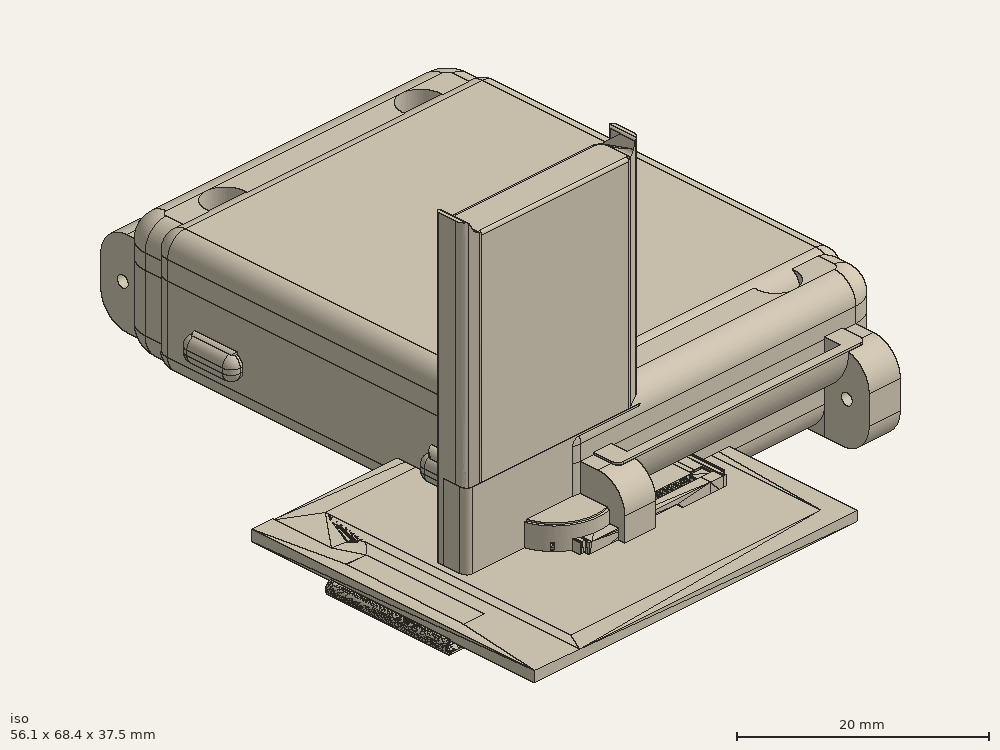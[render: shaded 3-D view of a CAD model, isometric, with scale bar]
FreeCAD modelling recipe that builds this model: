
FCSTD DOCUMENT  (FreeCAD 0.20R29177 +426 (Git))
Label: JJ-WATCHY_X
License: All rights reserved
LicenseURL: http://en.wikipedia.org/wiki/All_rights_reserved
objects: Part::Feature×80, App::Part×72, Sketcher::SketchObject×52, PartDesign::Pad×34, PartDesign::Pocket×27, PartDesign::Fillet×21, PartDesign::ShapeBinder×11, PartDesign::Body×8, PartDesign::Plane×4, Part::Part2DObjectPython×1, Part::Extrusion×1, PartDesign::FeatureBase×1, Mesh::Feature×1, Part::Fuse×1, Part::Cut×1
note: 324 computed .brp shape members not serialized (recipe doc carries the construction recipe); baked Part::Feature solids carry a one-line shape summary decoded from their .brp

FEATURE [Part::Feature] Part__Feature  label="SOLID (15)"
  shape: bbox 7.981 x 5.422 x 2.941 mm, 498 faces (baked)
FEATURE [App::Part] USB_Micro_B_Molex_47346_0001  label="USB_Micro-B_Molex_47346-0001"
  Group = -> [Part__Feature]
  Origin = -> Origin
  Placement = pos=(31.38,22.43,1.65) rot=(0,0,1;1.5708rad)
FEATURE [Part::Feature] Part__Feature001  label="SOLID"
  shape: bbox 1.6 x 0.8 x 0.8 mm, 28 faces (baked)
FEATURE [App::Part] C_0603_1608Metric
  Group = -> [Part__Feature001]
  Origin = -> Origin001
  Placement = pos=(5.16,37.71,1.65) rot=(0,0,1;0rad)
FEATURE [Part::Feature] Part__Feature002  label="SOLID (16)"
  shape: bbox 6.669 x 4.906 x 2.452 mm, 452 faces (baked)
FEATURE [App::Part] Button
  Group = -> [Part__Feature002]
  Origin = -> Origin002
  Placement = pos=(2.38,35.43,1.65) rot=(0,0,-1;1.5708rad)
FEATURE [Part::Feature] Part__Feature003  label="SOLID (16)001"
  shape: bbox 6.669 x 4.906 x 2.452 mm, 452 faces (baked)
FEATURE [App::Part] Button001
  Group = -> [Part__Feature003]
  Origin = -> Origin003
  Placement = pos=(2.38,8.73,1.65) rot=(0,0,-1;1.5708rad)
FEATURE [Part::Feature] Part__Feature004  label="SOLID (16)002"
  shape: bbox 6.669 x 4.906 x 2.452 mm, 452 faces (baked)
FEATURE [App::Part] Button002
  Group = -> [Part__Feature004]
  Origin = -> Origin004
  Placement = pos=(31.42,37.23,1.65) rot=(0,0,1;1.5708rad)
FEATURE [Part::Feature] Part__Feature005  label="SOLID (16)003"
  shape: bbox 6.669 x 4.906 x 2.452 mm, 452 faces (baked)
FEATURE [App::Part] Button003
  Group = -> [Part__Feature005]
  Origin = -> Origin005
  Placement = pos=(31.42,10.53,1.65) rot=(0,0,1;1.5708rad)
FEATURE [Part::Feature] Part__Feature006  label="SOLID (1)"
  shape: bbox 2 x 2 x 1.025 mm, 68 faces (baked)
FEATURE [App::Part] LGA_12_2x2mm_P0_5mm  label="LGA-12_2x2mm_P0.5mm"
  Group = -> [Part__Feature006]
  Origin = -> Origin006
  Placement = pos=(10.76,34.89,1.65) rot=(0,0,1;3.14159rad)
FEATURE [Part::Feature] Part__Feature007  label="COMPOUND (3)"
  shape: bbox 16.3 x 5.85 x 2.11 mm, 1280 faces, 17 solids (baked)
FEATURE [App::Part] FPC_24  label="FPC-24"
  Group = -> [Part__Feature007]
  Origin = -> Origin007
  Placement = pos=(11.025,19.09,1.65) rot=(0,0,1;0rad)
FEATURE [Part::Feature] Part__Feature008  label="SOLID (4)"
  shape: bbox 7.65 x 5.2 x 3.4 mm, 136 faces (baked)
FEATURE [App::Part] Molex_PicoBlade_53261_0271_1x02_1MP_P1_25mm_Horizontal  label="Molex_PicoBlade_53261-0271_1x02-1MP_P1.25mm_Horizontal"
  Group = -> [Part__Feature008]
  Origin = -> Origin008
  Placement = pos=(28.63,31.39,1.65) rot=(0,0,-1;1.5708rad)
FEATURE [Part::Feature] Part__Feature009  label="SOLID (2)"
  shape: bbox 1 x 0.5 x 0.35 mm, 26 faces (baked)
FEATURE [App::Part] R_0402_1005Metric
  Group = -> [Part__Feature009]
  Origin = -> Origin009
  Placement = pos=(31.7,28.28,1.65) rot=(0,0,1;1.5708rad)
FEATURE [Part::Feature] Part__Feature010  label="SOLID (5)"
  shape: bbox 4 x 4 x 1.1 mm, 158 faces (baked)
FEATURE [App::Part] QFN_24_1EP_4x4mm_P0_5mm_EP2_7x2_7mm  label="QFN-24-1EP_4x4mm_P0.5mm_EP2.7x2.7mm"
  Group = -> [Part__Feature010]
  Origin = -> Origin010
  Placement = pos=(25.76,24.38,1.65) rot=(0,0,1;0rad)
FEATURE [Part::Feature] Part__Feature011  label="SOLID (2)001"
  shape: bbox 1 x 0.5 x 0.35 mm, 26 faces (baked)
FEATURE [App::Part] R_0402_1005Metric001
  Group = -> [Part__Feature011]
  Origin = -> Origin011
  Placement = pos=(29.05,13.07,1.65) rot=(0,0,1;0rad)
FEATURE [Part::Feature] Part__Feature012  label="SOLID001"
  shape: bbox 1.6 x 0.8 x 0.8 mm, 28 faces (baked)
FEATURE [App::Part] C_0603_1608Metric001
  Group = -> [Part__Feature012]
  Origin = -> Origin012
  Placement = pos=(21.71,23.42,1.65) rot=(0,0,1;0rad)
FEATURE [Part::Feature] Part__Feature013  label="COMPOUND"
  shape: bbox 37.16 x 32.08 x 2.7 mm, 57 faces, 2 solids (baked)
FEATURE [App::Part] Display
  Group = -> [Part__Feature013]
  Origin = -> Origin013
  Placement = pos=(16.89,23.15,0.55) rot=(0.707107,0.707107,0;3.14159rad)
FEATURE [Part::Feature] Part__Feature014  label="SOLID002"
  shape: bbox 1.6 x 0.8 x 0.8 mm, 28 faces (baked)
FEATURE [App::Part] C_0603_1608Metric002
  Group = -> [Part__Feature014]
  Origin = -> Origin014
  Placement = pos=(15.42,35.06,1.65) rot=(0,0,1;1.5708rad)
FEATURE [Part::Feature] Part__Feature015  label="SOLID003"
  shape: bbox 1.6 x 0.8 x 0.8 mm, 28 faces (baked)
FEATURE [App::Part] C_0603_1608Metric003
  Group = -> [Part__Feature015]
  Origin = -> Origin015
  Placement = pos=(19.01,21.47,1.65) rot=(0,0,1;1.5708rad)
FEATURE [Part::Feature] Part__Feature016  label="SOLID (3)"
  shape: bbox 2 x 1.25 x 1.25 mm, 28 faces (baked)
FEATURE [App::Part] C_0805_2012Metric
  Group = -> [Part__Feature016]
  Origin = -> Origin016
  Placement = pos=(5.63,12.59,1.65) rot=(0,0,1;0rad)
FEATURE [Part::Feature] Part__Feature017  label="SOLID (3)001"
  shape: bbox 2 x 1.25 x 1.25 mm, 28 faces (baked)
FEATURE [App::Part] C_0805_2012Metric001
  Group = -> [Part__Feature017]
  Origin = -> Origin017
  Placement = pos=(6.63,6.34,1.65) rot=(0,0,1;0rad)
FEATURE [Part::Feature] Part__Feature018  label="SOLID004"
  shape: bbox 1.6 x 0.8 x 0.8 mm, 28 faces (baked)
FEATURE [App::Part] C_0603_1608Metric004
  Group = -> [Part__Feature018]
  Origin = -> Origin018
  Placement = pos=(13.81,21.47,1.65) rot=(0,0,1;1.5708rad)
FEATURE [Part::Feature] Part__Feature019  label="SOLID005"
  shape: bbox 1.6 x 0.8 x 0.8 mm, 28 faces (baked)
FEATURE [App::Part] C_0603_1608Metric005
  Group = -> [Part__Feature019]
  Origin = -> Origin019
  Placement = pos=(16.41,21.47,1.65) rot=(0,0,1;1.5708rad)
FEATURE [Part::Feature] Part__Feature020  label="SOLID006"
  shape: bbox 1.6 x 0.8 x 0.8 mm, 28 faces (baked)
FEATURE [App::Part] C_0603_1608Metric006
  Group = -> [Part__Feature020]
  Origin = -> Origin020
  Placement = pos=(17.71,21.47,1.65) rot=(0,0,1;1.5708rad)
FEATURE [Part::Feature] Part__Feature021  label="SOLID007"
  shape: bbox 1.6 x 0.8 x 0.8 mm, 28 faces (baked)
FEATURE [App::Part] C_0603_1608Metric007
  Group = -> [Part__Feature021]
  Origin = -> Origin021
  Placement = pos=(15.11,21.47,1.65) rot=(0,0,1;1.5708rad)
FEATURE [Part::Feature] Part__Feature022  label="SOLID008"
  shape: bbox 1.6 x 0.8 x 0.8 mm, 28 faces (baked)
FEATURE [App::Part] C_0603_1608Metric008
  Group = -> [Part__Feature022]
  Origin = -> Origin022
  Placement = pos=(12.46,21.47,1.65) rot=(0,0,1;1.5708rad)
FEATURE [Part::Feature] Part__Feature023  label="SOLID009"
  shape: bbox 1.6 x 0.8 x 0.8 mm, 28 faces (baked)
FEATURE [App::Part] C_0603_1608Metric009
  Group = -> [Part__Feature023]
  Origin = -> Origin023
  Placement = pos=(11.16,21.47,1.65) rot=(0,0,1;1.5708rad)
FEATURE [Part::Feature] Part__Feature024  label="SOLID (3)002"
  shape: bbox 2 x 1.25 x 1.25 mm, 28 faces (baked)
FEATURE [App::Part] C_0805_2012Metric002
  Group = -> [Part__Feature024]
  Origin = -> Origin024
  Placement = pos=(17.82,35.53,1.65) rot=(0,0,1;3.14159rad)
FEATURE [Part::Feature] Part__Feature025  label="SOLID (6)"
  shape: bbox 3.8 x 1.6 x 1.25 mm, 67 faces (baked)
FEATURE [App::Part] D_SOD_123  label="D_SOD-123"
  Group = -> [Part__Feature025]
  Origin = -> Origin025
  Placement = pos=(1.25,15.82,1.65) rot=(0,0,1;1.5708rad)
FEATURE [Part::Feature] Part__Feature026  label="SOLID (6)001"
  shape: bbox 3.8 x 1.6 x 1.25 mm, 67 faces (baked)
FEATURE [App::Part] D_SOD_123001  label="D_SOD-124"
  Group = -> [Part__Feature026]
  Origin = -> Origin026
  Placement = pos=(3.55,15.82,1.65) rot=(0,0,-1;1.5708rad)
FEATURE [Part::Feature] Part__Feature027  label="SOLID (6)002"
  shape: bbox 3.8 x 1.6 x 1.25 mm, 67 faces (baked)
FEATURE [App::Part] D_SOD_123002  label="D_SOD-125"
  Group = -> [Part__Feature027]
  Origin = -> Origin027
  Placement = pos=(5.85,15.82,1.65) rot=(0,0,-1;1.5708rad)
FEATURE [Part::Feature] Part__Feature028  label="SOLID (6)003"
  shape: bbox 3.8 x 1.6 x 1.25 mm, 67 faces (baked)
FEATURE [App::Part] D_SOD_123003  label="D_SOD-126"
  Group = -> [Part__Feature028]
  Origin = -> Origin028
  Placement = pos=(27.27,19.28,1.65) rot=(0,0,1;1.5708rad)
FEATURE [Part::Feature] Part__Feature029  label="SOLID (7)"
  shape: bbox 1.6 x 0.8 x 1.1 mm, 50 faces (baked)
FEATURE [App::Part] LED_0603_1608Metric
  Group = -> [Part__Feature029]
  Origin = -> Origin029
  Placement = pos=(33.04,30.53,1.65) rot=(0,0,1;1.5708rad)
FEATURE [Part::Feature] Part__Feature030  label="SOLID (8)"
  shape: bbox 3.5 x 1.6 x 1.1 mm, 27 faces (baked)
FEATURE [App::Part] D_SOD_123F  label="D_SOD-123F"
  Group = -> [Part__Feature030]
  Origin = -> Origin030
  Placement = pos=(4.91,34.705,1.65) rot=(0,0,-1;1.5708rad)
FEATURE [Part::Feature] Part__Feature031  label="SOLID (9)"
  shape: bbox 3.2 x 2.5 x 2.5 mm, 28 faces (baked)
FEATURE [App::Part] L_1210_3225Metric
  Group = -> [Part__Feature031]
  Origin = -> Origin031
  Placement = pos=(6.13,9.47,1.65) rot=(0,0,-1;1.5708rad)
FEATURE [Part::Feature] Part__Feature032  label="SOLID (10)"
  shape: bbox 2.5 x 3 x 1.2 mm, 76 faces (baked)
FEATURE [App::Part] SOT_23  label="SOT-23"
  Group = -> [Part__Feature032]
  Origin = -> Origin032
  Placement = pos=(28.1,9.03,1.65) rot=(0,0,-1;1.5708rad)
FEATURE [Part::Feature] Part__Feature033  label="SOLID (10)001"
  shape: bbox 2.5 x 3 x 1.2 mm, 76 faces (baked)
FEATURE [App::Part] SOT_23001  label="SOT-024"
  Group = -> [Part__Feature033]
  Origin = -> Origin033
  Placement = pos=(28.45,15.23,1.65) rot=(0,0,-1;1.5708rad)
FEATURE [Part::Feature] Part__Feature034  label="SOLID (10)002"
  shape: bbox 2.5 x 3 x 1.2 mm, 76 faces (baked)
FEATURE [App::Part] SOT_23002  label="SOT-025"
  Group = -> [Part__Feature034]
  Origin = -> Origin034
  Placement = pos=(7.81,35.31,1.65) rot=(0,0,1;3.14159rad)
FEATURE [Part::Feature] Part__Feature035  label="SOLID (2)002"
  shape: bbox 1 x 0.5 x 0.35 mm, 26 faces (baked)
FEATURE [App::Part] R_0402_1005Metric002
  Group = -> [Part__Feature035]
  Origin = -> Origin035
  Placement = pos=(16.97,34.19,1.65) rot=(0,0,1;3.14159rad)
FEATURE [Part::Feature] Part__Feature036  label="SOLID (2)003"
  shape: bbox 1 x 0.5 x 0.35 mm, 26 faces (baked)
FEATURE [App::Part] R_0402_1005Metric003
  Group = -> [Part__Feature036]
  Origin = -> Origin036
  Placement = pos=(22.55,26.67,1.65) rot=(0,0,1;1.5708rad)
FEATURE [Part::Feature] Part__Feature037  label="SOLID (2)004"
  shape: bbox 1 x 0.5 x 0.35 mm, 26 faces (baked)
FEATURE [App::Part] R_0402_1005Metric004
  Group = -> [Part__Feature037]
  Origin = -> Origin037
  Placement = pos=(23.91,27.48,1.65) rot=(0,0,1;3.14159rad)
FEATURE [Part::Feature] Part__Feature038  label="SOLID (2)005"
  shape: bbox 1 x 0.5 x 0.35 mm, 26 faces (baked)
FEATURE [App::Part] R_0402_1005Metric005
  Group = -> [Part__Feature038]
  Origin = -> Origin038
  Placement = pos=(27.15,13.07,1.65) rot=(0,0,1;3.14159rad)
FEATURE [Part::Feature] Part__Feature039  label="SOLID (2)006"
  shape: bbox 1 x 0.5 x 0.35 mm, 26 faces (baked)
FEATURE [App::Part] R_0402_1005Metric006
  Group = -> [Part__Feature039]
  Origin = -> Origin039
  Placement = pos=(28.66,36.44,1.65) rot=(0,0,1;0rad)
FEATURE [Part::Feature] Part__Feature040  label="SOLID (2)007"
  shape: bbox 1 x 0.5 x 0.35 mm, 26 faces (baked)
FEATURE [App::Part] R_0402_1005Metric007
  Group = -> [Part__Feature040]
  Origin = -> Origin040
  Placement = pos=(6.69,32.68,1.65) rot=(0,0,-1;1.5708rad)
FEATURE [Part::Feature] Part__Feature041  label="SOLID (2)008"
  shape: bbox 1 x 0.5 x 0.35 mm, 26 faces (baked)
FEATURE [App::Part] R_0402_1005Metric008
  Group = -> [Part__Feature041]
  Origin = -> Origin041
  Placement = pos=(29.05,11.28,1.65) rot=(0,0,1;3.14159rad)
FEATURE [Part::Feature] Part__Feature042  label="SOLID (2)009"
  shape: bbox 1 x 0.5 x 0.35 mm, 26 faces (baked)
FEATURE [App::Part] R_0402_1005Metric009
  Group = -> [Part__Feature042]
  Origin = -> Origin042
  Placement = pos=(27.15,11.28,1.65) rot=(0,0,1;3.14159rad)
FEATURE [Part::Feature] Part__Feature043  label="SOLID (2)010"
  shape: bbox 1 x 0.5 x 0.35 mm, 26 faces (baked)
FEATURE [App::Part] R_0402_1005Metric010
  Group = -> [Part__Feature043]
  Origin = -> Origin043
  Placement = pos=(4.35,6.34,1.65) rot=(0,0,1;1.5708rad)
FEATURE [Part::Feature] Part__Feature044  label="SOLID (2)011"
  shape: bbox 1 x 0.5 x 0.35 mm, 26 faces (baked)
FEATURE [App::Part] R_0402_1005Metric011
  Group = -> [Part__Feature044]
  Origin = -> Origin044
  Placement = pos=(30.8,28.28,1.65) rot=(0,0,1;1.5708rad)
FEATURE [Part::Feature] Part__Feature045  label="SOLID (2)012"
  shape: bbox 1 x 0.5 x 0.35 mm, 26 faces (baked)
FEATURE [App::Part] R_0402_1005Metric012
  Group = -> [Part__Feature045]
  Origin = -> Origin045
  Placement = pos=(29.32,17.4,1.65) rot=(0,0,1;3.14159rad)
FEATURE [Part::Feature] Part__Feature046  label="SOLID (2)013"
  shape: bbox 1 x 0.5 x 0.35 mm, 26 faces (baked)
FEATURE [App::Part] R_0402_1005Metric013
  Group = -> [Part__Feature046]
  Origin = -> Origin046
  Placement = pos=(33.24,28.28,1.65) rot=(0,0,-1;1.5708rad)
FEATURE [Part::Feature] Part__Feature047  label="SOLID (2)014"
  shape: bbox 1 x 0.5 x 0.35 mm, 26 faces (baked)
FEATURE [App::Part] R_0402_1005Metric014
  Group = -> [Part__Feature047]
  Origin = -> Origin047
  Placement = pos=(7.75,32.68,1.65) rot=(0,0,-1;1.5708rad)
FEATURE [Part::Feature] Part__Feature048  label="SOLID (13)"
  shape: bbox 7 x 7 x 0.77 mm, 302 faces (baked)
FEATURE [App::Part] QFN_48_1EP_7x7mm_P0_5mm_EP5_15x5_15mm  label="QFN-48-1EP_7x7mm_P0.5mm_EP5.15x5.15mm"
  Group = -> [Part__Feature048]
  Origin = -> Origin048
  Placement = pos=(17.7737,29.6588,1.65) rot=(0,0,-1;1.5708rad)
FEATURE [Part::Feature] Part__Feature049  label="SOLID (11)"
  shape: bbox 2.8 x 2.9 x 1.55 mm, 109 faces (baked)
FEATURE [App::Part] SOT_23_5  label="SOT-23-5"
  Group = -> [Part__Feature049]
  Origin = -> Origin049
  Placement = pos=(24.66,19.88,1.65) rot=(0,0,-1;1.5708rad)
FEATURE [Part::Feature] Part__Feature050  label="SOLID (11)001"
  shape: bbox 2.8 x 2.9 x 1.55 mm, 109 faces (baked)
FEATURE [App::Part] SOT_23_5001  label="SOT-23-006"
  Group = -> [Part__Feature050]
  Origin = -> Origin050
  Placement = pos=(32,15.93,1.65) rot=(0,0,-1;1.5708rad)
FEATURE [Part::Feature] Part__Feature051  label="SOLID (12)"
  shape: bbox 2 x 2 x 1.05 mm, 118 faces (baked)
FEATURE [App::Part] SOT_363_SC_70_6  label="SOT-363_SC-70-6"
  Group = -> [Part__Feature051]
  Origin = -> Origin051
  Placement = pos=(21.31,21.47,1.65) rot=(0,0,1;3.14159rad)
FEATURE [Part::Feature] Part__Feature052  label="SOLID (14)"
  shape: bbox 6 x 4.9 x 1.75 mm, 156 faces (baked)
FEATURE [App::Part] SOIC_8_3_9x4_9mm_P1_27mm  label="SOIC-8_3.9x4.9mm_P1.27mm"
  Group = -> [Part__Feature052]
  Origin = -> Origin052
  Placement = pos=(11.07,29.81,1.65) rot=(0,0,1;1.5708rad)
FEATURE [Part::Feature] Part__Feature053  label="SOLID (2)015"
  shape: bbox 1 x 0.5 x 0.35 mm, 26 faces (baked)
FEATURE [App::Part] R_0402_1005Metric015
  Group = -> [Part__Feature053]
  Origin = -> Origin053
  Placement = pos=(7.75,30.52,1.65) rot=(0,0,-1;1.5708rad)
FEATURE [Part::Feature] Part__Feature054  label="COMPOUND (1)"
  shape: bbox 13 x 10 x 2.5 mm, 15 faces, 3 solids (baked)
FEATURE [App::Part] PagerMotor
  Group = -> [Part__Feature054]
  Origin = -> Origin054
  Placement = pos=(5.45,22.955,5.15) rot=(0.819152,-0.573576,0;3.14159rad)
FEATURE [Part::Feature] Part__Feature055  label="COMPOUND (2)"
  shape: bbox 33.8 x 45.96 x 1 mm, 46 faces (baked)
FEATURE [App::Part] Watchy_Fixed_Dimensions_v1  label="Watchy Fixed Dimensions v1"
  Group = -> [USB_Micro_B_Molex_47346_0001,C_0603_1608Metric,Button,Button001,Button002,Button003,LGA_12_2x2mm_P0_5mm,FPC_24,Molex_PicoBlade_53261_0271_1x02_1MP_P1_25mm_Horizontal,R_0402_1005Metric,QFN_24_1EP_4x4mm_P0_5mm_EP2_7x2_7mm,R_0402_1005Metric001,C_0603_1608Metric001,Display,C_0603_1608Metric002,C_0603_1608Metric003,C_0805_2012Metric,C_0805_2012Metric001,C_0603_1608Metric004,C_0603_1608Metric005,+36 more]
  Origin = -> Origin055
  Placement = pos=(0,0,-0.43) rot=(0,0,1;0rad)
FEATURE [Sketcher::SketchObject] Sketch
  FullyConstrained = true
  MapMode = 5
  Placement = pos=(0,0,0) rot=(0,1,0;3.14159rad)
  Support = -> [XY_Plane056]
  sketch-geometry (4):
    g0: LineSegment StartX=-32.81 StartY=41.31 StartZ=0 EndX=-0.98 EndY=41.31 EndZ=0
    g1: LineSegment StartX=-0.98 StartY=41.31 StartZ=0 EndX=-0.98 EndY=10.07 EndZ=0
    g2: LineSegment StartX=-0.98 StartY=10.07 StartZ=0 EndX=-32.81 EndY=10.07 EndZ=0
    g3: LineSegment StartX=-32.81 StartY=10.07 StartZ=0 EndX=-32.81 EndY=41.31 EndZ=0
  constraints (12):
    c: Coincident(g0,g1)
    c: Coincident(g1,g2)
    c: Coincident(g2,g3)
    c: Coincident(g3,g0)
    c: Horizontal(g0)
    c: Horizontal(g2)
    c: Vertical(g1)
    c: Vertical(g3)
    c: DistanceX(g0,g0) = 31.83
    c: DistanceY(g1,g1) = 31.24
    c: DistanceY(g-1,g1) = 10.07
    c: DistanceX(g1,g-1) = 0.98
FEATURE [PartDesign::Pad] Pad
  Direction = (0,0,-1)
  Length = 1.5
  Length2 = 10
  Profile = -> Sketch
  ReferenceAxis = -> Sketch [N_Axis]
  Type = 0
FEATURE [PartDesign::Fillet] Fillet
  Base = -> Pad [Edge1,Edge2,Edge5,Edge8]
  BaseFeature = -> Pad
  Radius = 1
  SupportTransform = false
  UseAllEdges = false
FEATURE [PartDesign::Pocket] Pocket
  BaseFeature = -> Fillet
  Direction = (0,0,-1)
  Length = 0.9
  Length2 = 5
  Profile = -> Fillet [Face2]
  Type = 0
FEATURE [PartDesign::ShapeBinder] ReferencePocket
  Placement = pos=(0,0,-1.5) rot=(0,0,1;0rad)
  Support = -> [Pocket]
  TraceSupport = false
FEATURE [PartDesign::Plane] DatumPlane
  Length = 75.1964
  MapMode = 5
  Placement = pos=(0,0,-1.5) rot=(1,0,0;3.14159rad)
  ResizeMode = 0
  Support = -> [ReferencePocket]
  Width = 91.2964
FEATURE [Sketcher::SketchObject] Sketch001
  ExternalGeometry = -> [ReferencePocket]
  FullyConstrained = true
  MapMode = 5
  Placement = pos=(0,0,-1.5) rot=(1,0,0;3.14159rad)
  Support = -> [DatumPlane]
  sketch-geometry (5):
    g0: LineSegment StartX=-1.6 StartY=1.5 StartZ=0 EndX=35.4 EndY=1.5 EndZ=0
    g1: LineSegment StartX=35.4 StartY=1.5 StartZ=0 EndX=35.4 EndY=-47.5 EndZ=0
    g2: LineSegment StartX=35.4 StartY=-47.5 StartZ=0 EndX=-1.6 EndY=-47.5 EndZ=0
    g3: LineSegment StartX=-1.6 StartY=-47.5 StartZ=0 EndX=-1.6 EndY=1.5 EndZ=0
    g4: GeomPoint X=16.9 Y=-23 Z=0
  constraints (13):
    c: Coincident(g0,g1)
    c: Coincident(g1,g2)
    c: Coincident(g2,g3)
    c: Coincident(g3,g0)
    c: Horizontal(g0)
    c: Horizontal(g2)
    c: Vertical(g1)
    c: Vertical(g3)
    c: DistanceX(g0,g0) = 37
    c: DistanceY(g1,g1) = 49
    c: DistanceX(g-1,g4) = 16.9
    c: DistanceY(g4,g-1) = 23
    c: Symmetric(g2,g0,g4)
FEATURE [PartDesign::Pad] Pad001
  Direction = (0,0,-1)
  Length = 1
  Length2 = 8
  Placement = pos=(0,0,-1.5) rot=(1,0,0;3.14159rad)
  Profile = -> Sketch001
  ReferenceAxis = -> Sketch001 [N_Axis]
  Type = 4
FEATURE [Sketcher::SketchObject] Sketch002
  FullyConstrained = true
  MapMode = 5
  Placement = pos=(0,0,-2.5) rot=(1,0,0;3.14159rad)
  Support = -> [Pad001]
  sketch-geometry (5):
    g0: LineSegment StartX=3 StartY=-12.3 StartZ=0 EndX=31 EndY=-12.3 EndZ=0
    g1: LineSegment StartX=31 StartY=-12.3 StartZ=0 EndX=31 EndY=-39.3 EndZ=0
    g2: LineSegment StartX=31 StartY=-39.3 StartZ=0 EndX=3 EndY=-39.3 EndZ=0
    g3: LineSegment StartX=3 StartY=-39.3 StartZ=0 EndX=3 EndY=-12.3 EndZ=0
    g4: GeomPoint X=17 Y=-25.8 Z=0
  constraints (13):
    c: Coincident(g0,g1)
    c: Coincident(g1,g2)
    c: Coincident(g2,g3)
    c: Coincident(g3,g0)
    c: Horizontal(g0)
    c: Horizontal(g2)
    c: Vertical(g1)
    c: Vertical(g3)
    c: DistanceX(g0,g0) = 28
    c: DistanceY(g1,g1) = 27
    c: DistanceX(g-1,g4) = 17
    c: DistanceY(g4,g-1) = 25.8
    c: Symmetric(g2,g0,g4)
FEATURE [PartDesign::Pocket] Pocket001
  BaseFeature = -> Pad001
  Direction = (0,-1e-16,1)
  Length = 1
  Length2 = 5
  Placement = pos=(0,0,-1.5) rot=(1,0,0;3.14159rad)
  Profile = -> Sketch002
  ReferenceAxis = -> Sketch002 [N_Axis]
  Type = 0
FEATURE [Sketcher::SketchObject] Sketch003
  ExternalGeometry = -> [Pocket001]
  FullyConstrained = true
  MapMode = 5
  Placement = pos=(0,0,6.5) rot=(0,0,1;0rad)
  Support = -> [Pocket001]
  sketch-geometry (5):
    g0: LineSegment StartX=-0.6 StartY=46.5 StartZ=0 EndX=-0.6 EndY=-0.5 EndZ=0
    g1: LineSegment StartX=-0.6 StartY=-0.5 StartZ=0 EndX=34.4 EndY=-0.5 EndZ=0
    g2: LineSegment StartX=34.4 StartY=-0.5 StartZ=0 EndX=34.4 EndY=46.5 EndZ=0
    g3: LineSegment StartX=34.4 StartY=46.5 StartZ=0 EndX=-0.6 EndY=46.5 EndZ=0
    g4: Circle CenterX=16.9 CenterY=23 CenterZ=0 NormalX=0 NormalY=0 NormalZ=1 AngleXU=0 Radius=29.3002
  constraints (14):
    c: Coincident(g0,g1)
    c: Coincident(g1,g2)
    c: Coincident(g2,g3)
    c: Coincident(g3,g0)
    c: PointOnObject(g0,g4)
    c: PointOnObject(g1,g4)
    c: PointOnObject(g2,g4)
    c: PointOnObject(g3,g4)
    c: Horizontal(g3)
    c: Horizontal(g1)
    c: Vertical(g2)
    c: DistanceX(g3,g3) = 35
    c: DistanceY(g2,g2) = 47
    c: Symmetric(g-3,g-4,g4)
FEATURE [PartDesign::Pocket] Pocket002
  BaseFeature = -> Pocket001
  Direction = (0,2e-16,-1)
  Length = 7
  Length2 = 5
  Placement = pos=(0,0,-1.5) rot=(1,0,0;3.14159rad)
  Profile = -> Sketch003
  ReferenceAxis = -> Sketch003 [N_Axis]
  Type = 0
FEATURE [Sketcher::SketchObject] Sketch004
  ExternalGeometry = -> [ReferencePocket]
  FullyConstrained = true
  MapMode = 5
  Placement = pos=(0,-2e-16,-0.5) rot=(0,0,1;0rad)
  Support = -> [Pocket002]
  sketch-geometry (4):
    g0: LineSegment StartX=0.48 StartY=41.81 StartZ=0 EndX=33.31 EndY=41.81 EndZ=0
    g1: LineSegment StartX=33.31 StartY=41.81 StartZ=0 EndX=33.31 EndY=9.57 EndZ=0
    g2: LineSegment StartX=33.31 StartY=9.57 StartZ=0 EndX=0.48 EndY=9.57 EndZ=0
    g3: LineSegment StartX=0.48 StartY=9.57 StartZ=0 EndX=0.48 EndY=41.81 EndZ=0
  constraints (12):
    c: Coincident(g0,g1)
    c: Coincident(g1,g2)
    c: Coincident(g2,g3)
    c: Coincident(g3,g0)
    c: Horizontal(g0)
    c: Horizontal(g2)
    c: Vertical(g1)
    c: Vertical(g3)
    c: DistanceX(g0,g-4) = 0.5
    c: DistanceX(g-6,g0) = 0.5
    c: DistanceY(g-3,g0) = 0.5
    c: DistanceY(g1,g-5) = 0.5
FEATURE [PartDesign::Pocket] Pocket003
  BaseFeature = -> Pocket002
  Direction = (0,4e-16,-1)
  Length = 1
  Length2 = 5
  Placement = pos=(0,0,-1.5) rot=(1,0,0;3.14159rad)
  Profile = -> Sketch004
  ReferenceAxis = -> Sketch004 [N_Axis]
  Type = 0
FEATURE [Sketcher::SketchObject] Sketch005
  FullyConstrained = true
  MapMode = 5
  Placement = pos=(34.4,0,-1.5) rot=(0.57735,0.57735,-0.57735;4.18879rad)
  Support = -> [Pocket003]
  sketch-geometry (4):
    g0: LineSegment StartX=18.2 StartY=-2.15 StartZ=0 EndX=26.7 EndY=-2.15 EndZ=0
    g1: LineSegment StartX=26.7 StartY=-2.15 StartZ=0 EndX=26.7 EndY=-5.75 EndZ=0
    g2: LineSegment StartX=26.7 StartY=-5.75 StartZ=0 EndX=18.2 EndY=-5.75 EndZ=0
    g3: LineSegment StartX=18.2 StartY=-5.75 StartZ=0 EndX=18.2 EndY=-2.15 EndZ=0
  constraints (12):
    c: Coincident(g0,g1)
    c: Coincident(g1,g2)
    c: Coincident(g2,g3)
    c: Coincident(g3,g0)
    c: Horizontal(g0)
    c: Horizontal(g2)
    c: Vertical(g1)
    c: Vertical(g3)
    c: DistanceX(g2,g2) = 8.5
    c: DistanceY(g1,g1) = 3.6
    c: DistanceX(g-1,g0) = 18.2
    c: DistanceY(g0,g-1) = 2.15
FEATURE [PartDesign::Pocket] Pocket004
  BaseFeature = -> Pocket003
  Direction = (1,0,0)
  Length = 5
  Length2 = 5
  Placement = pos=(0,0,-1.5) rot=(1,0,0;3.14159rad)
  Profile = -> Sketch005
  ReferenceAxis = -> Sketch005 [N_Axis]
  Type = 0
FEATURE [Sketcher::SketchObject] Sketch006
  ExternalGeometry = -> [Pocket004]
  FullyConstrained = true
  MapMode = 5
  Placement = pos=(0,0,6.5) rot=(0,0,1;0rad)
  Support = -> [Pocket004]
  sketch-geometry (20):
    g0: LineSegment StartX=-1 StartY=37.83 StartZ=0 EndX=-0.6 EndY=37.83 EndZ=0
    g1: LineSegment StartX=-0.6 StartY=37.83 StartZ=0 EndX=-0.6 EndY=34.83 EndZ=0
    g2: LineSegment StartX=-0.6 StartY=34.83 StartZ=0 EndX=-1 EndY=34.83 EndZ=0
    g3: LineSegment StartX=-1 StartY=34.83 StartZ=0 EndX=-1 EndY=37.83 EndZ=0
    g4: LineSegment StartX=34.4 StartY=37.83 StartZ=0 EndX=34.8 EndY=37.83 EndZ=0
    g5: LineSegment StartX=34.8 StartY=37.83 StartZ=0 EndX=34.8 EndY=34.83 EndZ=0
    g6: LineSegment StartX=34.8 StartY=34.83 StartZ=0 EndX=34.4 EndY=34.83 EndZ=0
    g7: LineSegment StartX=34.4 StartY=34.83 StartZ=0 EndX=34.4 EndY=37.83 EndZ=0
    g8: LineSegment StartX=34.4 StartY=8.13 StartZ=0 EndX=34.8 EndY=8.13 EndZ=0
    g9: LineSegment StartX=34.8 StartY=8.13 StartZ=0 EndX=34.8 EndY=11.13 EndZ=0
    g10: LineSegment StartX=34.8 StartY=11.13 StartZ=0 EndX=34.4 EndY=11.13 EndZ=0
    g11: LineSegment StartX=34.4 StartY=11.13 StartZ=0 EndX=34.4 EndY=8.13 EndZ=0
    g12: LineSegment StartX=-1 StartY=11.13 StartZ=0 EndX=-0.6 EndY=11.13 EndZ=0
    g13: LineSegment StartX=-0.6 StartY=11.13 StartZ=0 EndX=-0.6 EndY=8.13 EndZ=0
    g14: LineSegment StartX=-0.6 StartY=8.13 StartZ=0 EndX=-1 EndY=8.13 EndZ=0
    g15: LineSegment StartX=-1 StartY=8.13 StartZ=0 EndX=-1 EndY=11.13 EndZ=0
    g16: Circle CenterX=-0.8 CenterY=9.63 CenterZ=0 NormalX=0 NormalY=0 NormalZ=1 AngleXU=0 Radius=1.51327
    g17: Circle CenterX=34.6 CenterY=9.63 CenterZ=0 NormalX=0 NormalY=0 NormalZ=1 AngleXU=0 Radius=1.51327
    g18: Circle CenterX=34.6 CenterY=36.33 CenterZ=0 NormalX=0 NormalY=0 NormalZ=1 AngleXU=0 Radius=1.51327
    g19: Circle CenterX=-0.8 CenterY=36.33 CenterZ=0 NormalX=0 NormalY=0 NormalZ=1 AngleXU=0 Radius=1.51327
  constraints (60):
    c: Coincident(g0,g1)
    c: Coincident(g1,g2)
    c: Coincident(g2,g3)
    c: Coincident(g3,g0)
    c: Horizontal(g0)
    c: Horizontal(g2)
    c: Vertical(g1)
    c: Vertical(g3)
    c: PointOnObject(g0,g-3)
    c: DistanceX(g0,g0) = 0.4
    c: DistanceY(g3,g3) = 3
    c: Coincident(g4,g5)
    c: Coincident(g5,g6)
    c: Coincident(g6,g7)
    c: Coincident(g7,g4)
    c: Horizontal(g4)
    c: Horizontal(g6)
    c: Vertical(g5)
    c: Vertical(g7)
    c: Coincident(g8,g9)
    c: Coincident(g9,g10)
    c: Coincident(g10,g11)
    c: Coincident(g11,g8)
    c: Horizontal(g8)
    c: Horizontal(g10)
    c: Vertical(g9)
    c: Vertical(g11)
    c: Coincident(g12,g13)
    c: Coincident(g13,g14)
    c: Coincident(g14,g15)
    c: Coincident(g15,g12)
    c: Horizontal(g12)
    c: Horizontal(g14)
    c: Vertical(g13)
    c: Vertical(g15)
    c: Equal(g0,g12)
    c: Equal(g12,g4)
    c: Equal(g4,g8)
    c: Equal(g3,g13)
    c: Equal(g13,g5)
    c: Equal(g5,g9)
    c: PointOnObject(g12,g-3)
    c: PointOnObject(g4,g-4)
    c: PointOnObject(g8,g-4)
    c: PointOnObject(g12,g16)
    c: PointOnObject(g12,g16)
    c: PointOnObject(g14,g16)
    c: DistanceY(g-1,g16) = 9.63
    c: PointOnObject(g9,g17)
    c: PointOnObject(g10,g17)
    c: PointOnObject(g8,g17)
    c: PointOnObject(g4,g18)
    c: PointOnObject(g4,g18)
    c: PointOnObject(g5,g18)
    c: PointOnObject(g0,g19)
    c: PointOnObject(g0,g19)
    c: PointOnObject(g2,g19)
    c: DistanceY(g-1,g19) = 36.33
    c: DistanceY(g-1,g18) = 36.33
    c: DistanceY(g-1,g17) = 9.63
FEATURE [PartDesign::Pocket] Pocket005
  BaseFeature = -> Pocket004
  Direction = (0,0,-1)
  Length = 5.5
  Length2 = 5
  Placement = pos=(0,0,-1.5) rot=(1,0,0;3.14159rad)
  Profile = -> Sketch006
  ReferenceAxis = -> Sketch006 [N_Axis]
  Type = 0
FEATURE [Sketcher::SketchObject] Sketch007
  FullyConstrained = true
  MapMode = 5
  Placement = pos=(-1.6,0,-1.5) rot=(0.57735,0.57735,-0.57735;4.18879rad)
  Support = -> [Pocket005]
  sketch-geometry (8):
    g0: LineSegment StartX=7.23 StartY=-3.5 StartZ=0 EndX=12.03 EndY=-3.5 EndZ=0
    g1: LineSegment StartX=12.03 StartY=-3.5 StartZ=0 EndX=12.03 EndY=-5.3 EndZ=0
    g2: LineSegment StartX=12.03 StartY=-5.3 StartZ=0 EndX=7.23 EndY=-5.3 EndZ=0
    g3: LineSegment StartX=7.23 StartY=-5.3 StartZ=0 EndX=7.23 EndY=-3.5 EndZ=0
    g4: LineSegment StartX=33.9 StartY=-3.1 StartZ=0 EndX=38.7 EndY=-3.1 EndZ=0
    g5: LineSegment StartX=38.7 StartY=-3.1 StartZ=0 EndX=38.7 EndY=-4.9 EndZ=0
    g6: LineSegment StartX=38.7 StartY=-4.9 StartZ=0 EndX=33.9 EndY=-4.9 EndZ=0
    g7: LineSegment StartX=33.9 StartY=-4.9 StartZ=0 EndX=33.9 EndY=-3.1 EndZ=0
  constraints (24):
    c: Coincident(g0,g1)
    c: Coincident(g1,g2)
    c: Coincident(g2,g3)
    c: Coincident(g3,g0)
    c: Horizontal(g0)
    c: Horizontal(g2)
    c: Vertical(g1)
    c: Vertical(g3)
    c: Coincident(g4,g5)
    c: Coincident(g5,g6)
    c: Coincident(g6,g7)
    c: Coincident(g7,g4)
    c: Horizontal(g4)
    c: Horizontal(g6)
    c: Vertical(g5)
    c: Vertical(g7)
    c: DistanceX(g2,g2) = 4.8
    c: DistanceY(g1,g1) = 1.8
    c: Equal(g1,g7)
    c: Equal(g2,g6)
    c: DistanceY(g0,g-1) = 3.5
    c: DistanceY(g4,g-1) = 3.1
    c: DistanceX(g-1,g0) = 7.23
    c: DistanceX(g-1,g4) = 33.9
FEATURE [PartDesign::Pad] Pad002
  BaseFeature = -> Pocket005
  Direction = (-1,0,0)
  Length = 1
  Length2 = 10
  Placement = pos=(0,0,-1.5) rot=(1,0,0;3.14159rad)
  Profile = -> Sketch007
  ReferenceAxis = -> Sketch007 [N_Axis]
  Type = 0
FEATURE [Sketcher::SketchObject] Sketch008
  ExternalGeometry = -> [Pad002]
  FullyConstrained = true
  MapMode = 5
  Placement = pos=(35.4,0,-1.5) rot=(0.57735,-0.57735,0.57735;4.18879rad)
  Support = -> [Pad002]
  sketch-geometry (8):
    g0: LineSegment StartX=-12.03 StartY=-3.5 StartZ=0 EndX=-7.23 EndY=-3.5 EndZ=0
    g1: LineSegment StartX=-7.23 StartY=-3.5 StartZ=0 EndX=-7.23 EndY=-5.3 EndZ=0
    g2: LineSegment StartX=-7.23 StartY=-5.3 StartZ=0 EndX=-12.03 EndY=-5.3 EndZ=0
    g3: LineSegment StartX=-12.03 StartY=-5.3 StartZ=0 EndX=-12.03 EndY=-3.5 EndZ=0
    g4: LineSegment StartX=-38.7 StartY=-3.1 StartZ=0 EndX=-33.9 EndY=-3.1 EndZ=0
    g5: LineSegment StartX=-33.9 StartY=-3.1 StartZ=0 EndX=-33.9 EndY=-4.9 EndZ=0
    g6: LineSegment StartX=-33.9 StartY=-4.9 StartZ=0 EndX=-38.7 EndY=-4.9 EndZ=0
    g7: LineSegment StartX=-38.7 StartY=-4.9 StartZ=0 EndX=-38.7 EndY=-3.1 EndZ=0
  constraints (20):
    c: Coincident(g0,g1)
    c: Coincident(g1,g2)
    c: Coincident(g2,g3)
    c: Coincident(g3,g0)
    c: Horizontal(g0)
    c: Horizontal(g2)
    c: Vertical(g1)
    c: Vertical(g3)
    c: Coincident(g0,g-4)
    c: Coincident(g1,g-6)
    c: Coincident(g4,g5)
    c: Coincident(g5,g6)
    c: Coincident(g6,g7)
    c: Coincident(g7,g4)
    c: Horizontal(g4)
    c: Horizontal(g6)
    c: Vertical(g5)
    c: Vertical(g7)
    c: Coincident(g4,g-8)
    c: Coincident(g5,g-7)
FEATURE [PartDesign::Pad] Pad003
  BaseFeature = -> Pad002
  Direction = (1,0,0)
  Length = 1
  Length2 = 10
  Placement = pos=(0,0,-1.5) rot=(1,0,0;3.14159rad)
  Profile = -> Sketch008
  ReferenceAxis = -> Sketch008 [N_Axis]
  Type = 0
FEATURE [PartDesign::Fillet] Fillet001
  Base = -> Pad003 [Edge5,Edge105,Edge18,Edge124,Edge1,Edge2,Edge116,Edge103]
  BaseFeature = -> Pad003
  Placement = pos=(0,0,-1.5) rot=(1,0,0;3.14159rad)
  Radius = 3
  SupportTransform = false
  UseAllEdges = false
FEATURE [PartDesign::Fillet] Fillet002
  Base = -> Fillet001 [Edge41]
  BaseFeature = -> Fillet001
  Placement = pos=(0,0,-1.5) rot=(1,0,0;3.14159rad)
  Radius = 3
  SupportTransform = false
  UseAllEdges = false
FEATURE [PartDesign::Fillet] Fillet003
  Base = -> Fillet002 [Edge60,Edge59,Edge58,Edge61]
  BaseFeature = -> Fillet002
  Placement = pos=(0,0,-1.5) rot=(1,0,0;3.14159rad)
  Radius = 0.2
  SupportTransform = false
  UseAllEdges = false
FEATURE [PartDesign::ShapeBinder] ReferenceFillet003
  Placement = pos=(0,0,-1.5) rot=(1,0,0;3.14159rad)
  Support = -> [Fillet003]
  TraceSupport = false
FEATURE [PartDesign::Plane] DatumPlane001
  Length = 73.6348
  MapMode = 5
  Placement = pos=(0,0,6.5) rot=(0,0,1;0rad)
  ResizeMode = 0
  Support = -> [ReferenceFillet003]
  Width = 85.7348
FEATURE [Sketcher::SketchObject] Sketch009
  ExternalGeometry = -> [ReferenceFillet003]
  FullyConstrained = true
  MapMode = 5
  Placement = pos=(0,0,6.5) rot=(0,0,1;0rad)
  Support = -> [DatumPlane001]
  sketch-geometry (8):
    g0: LineSegment StartX=1.4 StartY=47.5 StartZ=0 EndX=32.4 EndY=47.5 EndZ=0
    g1: LineSegment StartX=-1.6 StartY=44.5 StartZ=0 EndX=-1.6 EndY=1.5 EndZ=0
    g2: LineSegment StartX=35.4 StartY=44.5 StartZ=0 EndX=35.4 EndY=1.5 EndZ=0
    g3: LineSegment StartX=1.4 StartY=-1.5 StartZ=0 EndX=32.4 EndY=-1.5 EndZ=0
    g4: ArcOfCircle CenterX=1.4 CenterY=1.5 CenterZ=0 NormalX=0 NormalY=0 NormalZ=1 AngleXU=0 Radius=3 StartAngle=3.14159 EndAngle=4.71239
    g5: ArcOfCircle CenterX=32.4 CenterY=1.5 CenterZ=0 NormalX=0 NormalY=0 NormalZ=1 AngleXU=0 Radius=3 StartAngle=4.71239 EndAngle=6.28319
    g6: ArcOfCircle CenterX=1.4 CenterY=44.5 CenterZ=0 NormalX=0 NormalY=0 NormalZ=1 AngleXU=0 Radius=3 StartAngle=1.5708 EndAngle=3.14159
    g7: ArcOfCircle CenterX=32.4 CenterY=44.5 CenterZ=0 NormalX=0 NormalY=0 NormalZ=1 AngleXU=0 Radius=3 StartAngle=3e-16 EndAngle=1.5708
  constraints (20):
    c: Coincident(g0,g-4)
    c: Coincident(g0,g-6)
    c: Coincident(g1,g-5)
    c: Coincident(g1,g-7)
    c: Coincident(g2,g-10)
    c: Coincident(g2,g-10)
    c: Coincident(g3,g-8)
    c: Coincident(g3,g-9)
    c: Coincident(g4,g-7)
    c: Coincident(g4,g1)
    c: Coincident(g4,g3)
    c: Coincident(g5,g-9)
    c: Coincident(g5,g2)
    c: Coincident(g5,g3)
    c: Coincident(g6,g-4)
    c: Coincident(g6,g1)
    c: Coincident(g6,g0)
    c: Coincident(g7,g-6)
    c: Coincident(g7,g0)
    c: Coincident(g7,g2)
FEATURE [PartDesign::Pad] Pad004
  Direction = (0,-4e-16,1)
  Length = 4
  Length2 = 10
  Placement = pos=(0,-2.9e-15,6.5) rot=(0,0,1;0rad)
  Profile = -> Sketch009
  ReferenceAxis = -> Sketch009 [N_Axis]
  Type = 0
FEATURE [PartDesign::Fillet] Fillet004
  Base = -> Pad004 [Edge7]
  BaseFeature = -> Pad004
  Placement = pos=(0,-2.9e-15,6.5) rot=(0,0,1;0rad)
  Radius = 2.4
  SupportTransform = false
  UseAllEdges = false
FEATURE [Sketcher::SketchObject] Sketch010
  ExternalGeometry = -> [ReferenceFillet003]
  FullyConstrained = true
  MapMode = 5
  Placement = pos=(0,-2.9e-15,6.5) rot=(1,0,0;3.14159rad)
  Support = -> [Fillet004]
  sketch-geometry (8):
    g0: ArcOfCircle CenterX=2.4 CenterY=-2.5 CenterZ=0 NormalX=0 NormalY=0 NormalZ=1 AngleXU=0 Radius=2 StartAngle=1.5708 EndAngle=3.14159
    g1: ArcOfCircle CenterX=31.4 CenterY=-2.5 CenterZ=0 NormalX=0 NormalY=0 NormalZ=1 AngleXU=0 Radius=2 StartAngle=0 EndAngle=1.5708
    g2: ArcOfCircle CenterX=31.4 CenterY=-43.5 CenterZ=0 NormalX=0 NormalY=0 NormalZ=1 AngleXU=0 Radius=2 StartAngle=4.71239 EndAngle=6.28319
    g3: ArcOfCircle CenterX=2.4 CenterY=-43.5 CenterZ=0 NormalX=0 NormalY=0 NormalZ=1 AngleXU=0 Radius=2 StartAngle=3.14159 EndAngle=4.7124
    g4: LineSegment StartX=0.4 StartY=-2.5 StartZ=0 EndX=0.4 EndY=-43.5 EndZ=0
    g5: LineSegment StartX=2.4 StartY=-0.5 StartZ=0 EndX=31.4 EndY=-0.5 EndZ=0
    g6: LineSegment StartX=33.4 StartY=-2.5 StartZ=0 EndX=33.4 EndY=-43.5 EndZ=0
    g7: LineSegment StartX=31.4 StartY=-45.5 StartZ=0 EndX=2.40002 EndY=-45.5 EndZ=0
  constraints (17):
    c: Coincident(g7,g3)
    c: Vertical(g6)
    c: Horizontal(g5)
    c: Vertical(g4)
    c: Horizontal(g7)
    c: DistanceX(g-6,g3) = 1
    c: Coincident(g3,g-6)
    c: Coincident(g0,g-5)
    c: Coincident(g1,g-4)
    c: Coincident(g2,g-3)
    c: Tangent(g4,g3) = -1.5708
    c: Tangent(g4,g0) = -1.5708
    c: Tangent(g5,g0) = 1.5708
    c: Tangent(g5,g1) = 1.5708
    c: Tangent(g6,g1) = 1.5708
    c: Tangent(g6,g2) = 1.5708
    c: Tangent(g7,g2) = 1.5708
FEATURE [PartDesign::Pocket] Pocket006
  BaseFeature = -> Fillet004
  Direction = (0,-7e-16,1)
  Length = 3
  Length2 = 5
  Placement = pos=(0,-2.9e-15,6.5) rot=(0,0,1;0rad)
  Profile = -> Sketch010
  ReferenceAxis = -> Sketch010 [N_Axis]
  Type = 0
FEATURE [Sketcher::SketchObject] Sketch011
  ExternalGeometry = -> [Fillet003]
  FullyConstrained = true
  MapMode = 5
  Placement = pos=(0,-1.5,-1.5) rot=(0,0.707107,-0.707107;3.14159rad)
  Support = -> [Fillet003]
  sketch-geometry (8):
    g0: LineSegment StartX=-32.4 StartY=-8 StartZ=0 EndX=-28.9 EndY=-8 EndZ=0
    g1: LineSegment StartX=-28.9 StartY=-8 StartZ=0 EndX=-28.9 EndY=1 EndZ=0
    g2: LineSegment StartX=-28.9 StartY=1 StartZ=0 EndX=-32.4 EndY=1 EndZ=0
    g3: LineSegment StartX=-32.4 StartY=1 StartZ=0 EndX=-32.4 EndY=-8 EndZ=0
    g4: LineSegment StartX=-1.4 StartY=-8 StartZ=0 EndX=-4.9 EndY=-8 EndZ=0
    g5: LineSegment StartX=-4.9 StartY=-8 StartZ=0 EndX=-4.9 EndY=1 EndZ=0
    g6: LineSegment StartX=-4.9 StartY=1 StartZ=0 EndX=-1.4 EndY=1 EndZ=0
    g7: LineSegment StartX=-1.4 StartY=1 StartZ=0 EndX=-1.4 EndY=-8 EndZ=0
  constraints (22):
    c: Coincident(g0,g1)
    c: Coincident(g1,g2)
    c: Coincident(g2,g3)
    c: Coincident(g3,g0)
    c: Horizontal(g0)
    c: Horizontal(g2)
    c: Vertical(g1)
    c: Vertical(g3)
    c: Coincident(g0,g-3)
    c: PointOnObject(g1,g-5)
    c: Coincident(g4,g5)
    c: Coincident(g5,g6)
    c: Coincident(g6,g7)
    c: Coincident(g7,g4)
    c: Horizontal(g4)
    c: Horizontal(g6)
    c: Vertical(g5)
    c: Vertical(g7)
    c: Coincident(g4,g-4)
    c: PointOnObject(g5,g-5)
    c: DistanceX(g2,g2) = 3.5
    c: Equal(g6,g2)
FEATURE [PartDesign::Pad] Pad005
  BaseFeature = -> Fillet003
  Direction = (0,-1,-4e-16)
  Length = 5
  Length2 = 10
  Placement = pos=(0,0,-1.5) rot=(1,0,0;3.14159rad)
  Profile = -> Sketch011
  ReferenceAxis = -> Sketch011 [N_Axis]
  Type = 0
FEATURE [PartDesign::Pad] Pad006
  BaseFeature = -> Pad005
  Direction = (0,1,6e-16)
  Length = 3
  Length2 = 10
  Placement = pos=(0,0,-1.5) rot=(1,0,0;3.14159rad)
  Profile = -> Pad005 [Face18]
  Type = 0
FEATURE [PartDesign::Pad] Pad007
  BaseFeature = -> Pad006
  Direction = (0,1,7e-16)
  Length = 3
  Length2 = 10
  Placement = pos=(0,0,-1.5) rot=(1,0,0;3.14159rad)
  Profile = -> Pad006 [Face21]
  Type = 0
FEATURE [PartDesign::Fillet] Fillet005
  Base = -> Pad007 [Edge78,Edge70,Edge166,Edge161]
  BaseFeature = -> Pad007
  Placement = pos=(0,0,-1.5) rot=(1,0,0;3.14159rad)
  Radius = 3
  SupportTransform = false
  UseAllEdges = false
FEATURE [Sketcher::SketchObject] Sketch012
  ExternalGeometry = -> [Fillet005]
  FullyConstrained = true
  MapMode = 5
  Placement = pos=(0,47.5,-1.5) rot=(-1,0,0;1.5708rad)
  Support = -> [Fillet005]
  sketch-geometry (8):
    g0: LineSegment StartX=1.4 StartY=-8 StartZ=0 EndX=4.9 EndY=-8 EndZ=0
    g1: LineSegment StartX=4.9 StartY=-8 StartZ=0 EndX=4.9 EndY=1 EndZ=0
    g2: LineSegment StartX=4.9 StartY=1 StartZ=0 EndX=1.4 EndY=1 EndZ=0
    g3: LineSegment StartX=1.4 StartY=1 StartZ=0 EndX=1.4 EndY=-8 EndZ=0
    g4: LineSegment StartX=32.4 StartY=-8 StartZ=0 EndX=28.9 EndY=-8 EndZ=0
    g5: LineSegment StartX=28.9 StartY=-8 StartZ=0 EndX=28.9 EndY=1 EndZ=0
    g6: LineSegment StartX=28.9 StartY=1 StartZ=0 EndX=32.4 EndY=1 EndZ=0
    g7: LineSegment StartX=32.4 StartY=1 StartZ=0 EndX=32.4 EndY=-8 EndZ=0
  constraints (22):
    c: Coincident(g0,g1)
    c: Coincident(g1,g2)
    c: Coincident(g2,g3)
    c: Coincident(g3,g0)
    c: Horizontal(g0)
    c: Horizontal(g2)
    c: Vertical(g1)
    c: Vertical(g3)
    c: Coincident(g0,g-4)
    c: PointOnObject(g1,g-3)
    c: Coincident(g4,g5)
    c: Coincident(g5,g6)
    c: Coincident(g6,g7)
    c: Coincident(g7,g4)
    c: Horizontal(g4)
    c: Horizontal(g6)
    c: Vertical(g5)
    c: Vertical(g7)
    c: Coincident(g4,g-5)
    c: PointOnObject(g5,g-3)
    c: DistanceX(g2,g2) = 3.5
    c: Equal(g6,g2)
FEATURE [PartDesign::Pad] Pad008
  BaseFeature = -> Fillet005
  Direction = (0,1,7e-16)
  Length = 5
  Length2 = 10
  Placement = pos=(0,0,-1.5) rot=(1,0,0;3.14159rad)
  Profile = -> Sketch012
  ReferenceAxis = -> Sketch012 [N_Axis]
  Type = 0
FEATURE [PartDesign::Pad] Pad009
  BaseFeature = -> Pad008
  Direction = (0,-1,-9e-16)
  Length = 3
  Length2 = 10
  Placement = pos=(0,0,-1.5) rot=(1,0,0;3.14159rad)
  Profile = -> Pad008 [Face68,Face67]
  Type = 0
FEATURE [PartDesign::Fillet] Fillet006
  Base = -> Pad009 [Edge247,Edge241,Edge143,Edge148]
  BaseFeature = -> Pad009
  Placement = pos=(0,0,-1.5) rot=(1,0,0;3.14159rad)
  Radius = 3
  SupportTransform = false
  UseAllEdges = false
FEATURE [PartDesign::Fillet] Fillet007
  Base = -> Fillet006 [Edge234,Edge247,Edge246,Edge244,Edge242,Edge213,Edge218,Edge217,Edge215,Edge226,Edge221,Edge225,Edge223,Edge239,Edge238,Edge236,Edge230,Edge228,Edge231,Edge229]
  BaseFeature = -> Fillet006
  Placement = pos=(0,0,-1.5) rot=(1,0,0;3.14159rad)
  Radius = 0.8
  SupportTransform = false
  UseAllEdges = false
FEATURE [Sketcher::SketchObject] Sketch014
  ExternalGeometry = -> [Fillet007]
  FullyConstrained = true
  MapMode = 5
  Placement = pos=(32.4,0,-1.5) rot=(0.57735,-0.57735,0.57735;4.18879rad)
  Support = -> [Fillet007]
  sketch-geometry (2):
    g0: Circle CenterX=4 CenterY=-3.5 CenterZ=0 NormalX=0 NormalY=0 NormalZ=1 AngleXU=0 Radius=0.6
    g1: Circle CenterX=-50 CenterY=-3.5 CenterZ=0 NormalX=0 NormalY=0 NormalZ=1 AngleXU=0 Radius=0.6
  constraints (6):
    c: Diameter(g0) = 1.2
    c: Equal(g1,g0)
    c: DistanceY(g0,g-3) = 1.5
    c: DistanceX(g0,g-3) = 2.5
    c: DistanceY(g1,g-4) = 1.5
    c: DistanceX(g-4,g1) = 2.5
FEATURE [PartDesign::Pocket] Pocket007
  BaseFeature = -> Fillet007
  Direction = (-1,0,0)
  Length = 5
  Length2 = 5
  Placement = pos=(0,0,-1.5) rot=(1,0,0;3.14159rad)
  Profile = -> Sketch014
  ReferenceAxis = -> Sketch014 [N_Axis]
  Type = 1
FEATURE [PartDesign::Pad] Pad010
  BaseFeature = -> Pocket007
  Direction = (0,-1.4e-15,1)
  Length = 1
  Length2 = 10
  Placement = pos=(0,0,-1.5) rot=(1,0,0;3.14159rad)
  Profile = -> Pocket007 [Face64]
  Type = 0
FEATURE [Sketcher::SketchObject] Sketch015
  ExternalGeometry = -> [Pad010]
  FullyConstrained = true
  MapMode = 5
  Placement = pos=(0,-1e-15,0.5) rot=(0,0,1;0rad)
  sketch-geometry (4):
    g0: LineSegment StartX=0.48 StartY=9.57 StartZ=0 EndX=33.31 EndY=9.57 EndZ=0
    g1: LineSegment StartX=33.31 StartY=9.57 StartZ=0 EndX=33.31 EndY=3.87 EndZ=0
    g2: LineSegment StartX=33.31 StartY=3.87 StartZ=0 EndX=0.48 EndY=3.87 EndZ=0
    g3: LineSegment StartX=0.48 StartY=3.87 StartZ=0 EndX=0.48 EndY=9.57 EndZ=0
  constraints (10):
    c: Coincident(g0,g1)
    c: Coincident(g1,g2)
    c: Coincident(g2,g3)
    c: Coincident(g3,g0)
    c: Horizontal(g2)
    c: Vertical(g1)
    c: Vertical(g3)
    c: Coincident(g0,g-3)
    c: DistanceY(g3,g3) = 5.7
    c: Coincident(g0,g-3)
FEATURE [PartDesign::Pocket] Pocket008
  BaseFeature = -> Pad010
  Direction = (0,0,-1)
  Length = 1.52
  Length2 = 5
  Placement = pos=(0,0,-1.5) rot=(1,0,0;3.14159rad)
  Profile = -> Sketch015
  ReferenceAxis = -> Sketch015 [N_Axis]
  Type = 0
FEATURE [PartDesign::ShapeBinder] ShapeBinder
  Support = -> [Part__Feature055]
  TraceSupport = false
FEATURE [Sketcher::SketchObject] Sketch016
  ExternalGeometry = -> [ShapeBinder]
  FullyConstrained = true
  MapMode = 5
  Placement = pos=(0,-1e-15,0.5) rot=(0,0,1;0rad)
  sketch-geometry (8):
    g0: ArcOfCircle CenterX=3.9 CenterY=42.96 CenterZ=0 NormalX=0 NormalY=0 NormalZ=1 AngleXU=0 Radius=0.8 StartAngle=1.5708 EndAngle=4.71239
    g1: ArcOfCircle CenterX=29.9 CenterY=42.96 CenterZ=0 NormalX=0 NormalY=0 NormalZ=1 AngleXU=0 Radius=0.8 StartAngle=4.71239 EndAngle=7.85398
    g2: LineSegment StartX=3.9 StartY=43.76 StartZ=0 EndX=29.9 EndY=43.76 EndZ=0
    g3: LineSegment StartX=29.9 StartY=42.16 StartZ=0 EndX=3.9 EndY=42.16 EndZ=0
    g4: ArcOfCircle CenterX=3.9 CenterY=3 CenterZ=0 NormalX=0 NormalY=0 NormalZ=1 AngleXU=0 Radius=0.8 StartAngle=1.5708 EndAngle=4.71239
    g5: ArcOfCircle CenterX=29.9 CenterY=3 CenterZ=0 NormalX=0 NormalY=0 NormalZ=1 AngleXU=0 Radius=0.8 StartAngle=4.71239 EndAngle=7.85398
    g6: LineSegment StartX=3.9 StartY=3.8 StartZ=0 EndX=29.9 EndY=3.8 EndZ=0
    g7: LineSegment StartX=29.9 StartY=2.2 StartZ=0 EndX=3.9 EndY=2.2 EndZ=0
  constraints (18):
    c: Coincident(g0,g-5)
    c: Diameter(g0) = 1.6
    c: Coincident(g1,g-6)
    c: Equal(g0,g1)
    c: Coincident(g2,g1)
    c: Horizontal(g2)
    c: Coincident(g3,g1)
    c: Horizontal(g3)
    c: Tangent(g3,g0) = 1.5708
    c: Tangent(g2,g0) = 1.5708
    c: Coincident(g4,g-8)
    c: Coincident(g5,g-10)
    c: Equal(g4,g5)
    c: Tangent(g7,g4) = 1.5708
    c: Tangent(g6,g4) = 1.5708
    c: Tangent(g6,g5) = 1.5708
    c: Tangent(g7,g5) = 1.5708
    c: Equal(g4,g0)
FEATURE [PartDesign::Pad] Pad011
  BaseFeature = -> Pocket008
  Direction = (0,-1e-15,1)
  Length = 4
  Length2 = 10
  Placement = pos=(0,0,-1.5) rot=(1,0,0;3.14159rad)
  Profile = -> Sketch016
  ReferenceAxis = -> Sketch016 [N_Axis]
  Type = 0
FEATURE [PartDesign::ShapeBinder] ShapeBinder001
  Support = -> [Pad011]
  TraceSupport = false
FEATURE [Sketcher::SketchObject] Sketch020
  FullyConstrained = false
  MapMode = 5
  Placement = pos=(0,-1.2e-14,4.5) rot=(0,0,1;0rad)
  sketch-geometry (6):
    g0: Circle CenterX=5.9 CenterY=42.96 CenterZ=0 NormalX=0 NormalY=0 NormalZ=1 AngleXU=0 Radius=0.9
    g1: Circle CenterX=27.9 CenterY=42.96 CenterZ=0 NormalX=0 NormalY=0 NormalZ=1 AngleXU=0 Radius=0.9
    g2: Circle CenterX=5.9 CenterY=3 CenterZ=0 NormalX=0 NormalY=0 NormalZ=1 AngleXU=0 Radius=0.9
    g3: Circle CenterX=27.9 CenterY=3 CenterZ=0 NormalX=0 NormalY=0 NormalZ=1 AngleXU=0 Radius=0.9
    g4: LineSegment StartX=3.9 StartY=3 StartZ=0 EndX=29.9 EndY=3 EndZ=0
    g5: LineSegment StartX=3.9 StartY=42.96 StartZ=0 EndX=29.9 EndY=42.96 EndZ=0
  constraints (12):
    c: PointOnObject(g1,g5)
    c: PointOnObject(g0,g5)
    c: PointOnObject(g2,g4)
    c: PointOnObject(g3,g4)
    c: DistanceX(g5,g0) = 2
    c: DistanceX(g1,g5) = 2
    c: DistanceX(g4,g2) = 2
    c: DistanceX(g3,g4) = 2
    c: Diameter(g0) = 1.8
    c: Equal(g0,g1)
    c: Equal(g1,g3)
    c: Equal(g3,g2)
FEATURE [PartDesign::Pocket] Pocket011
  BaseFeature = -> Pad011
  Direction = (0,2e-15,-1)
  Length = 3
  Length2 = 5
  Placement = pos=(0,0,-1.5) rot=(1,0,0;3.14159rad)
  Profile = -> Sketch020
  ReferenceAxis = -> Sketch020 [N_Axis]
  Type = 0
FEATURE [Sketcher::SketchObject] Sketch021
  FullyConstrained = false
  MapMode = 5
  Placement = pos=(0,-8e-15,6.5) rot=(1,0,0;3.14159rad)
  sketch-geometry (16):
    g0: ArcOfCircle CenterX=2.4 CenterY=-2.5 CenterZ=0 NormalX=0 NormalY=0 NormalZ=1 AngleXU=0 Radius=2.65 StartAngle=1.5708 EndAngle=3.1416
    g1: LineSegment StartX=2.4 StartY=0.15 StartZ=0 EndX=31.4 EndY=0.15 EndZ=0
    g2: ArcOfCircle CenterX=31.4 CenterY=-2.5 CenterZ=0 NormalX=0 NormalY=0 NormalZ=1 AngleXU=0 Radius=2.65 StartAngle=0 EndAngle=1.5708
    g3: LineSegment StartX=34.05 StartY=-2.5 StartZ=0 EndX=34.05 EndY=-43.5 EndZ=0
    g4: ArcOfCircle CenterX=31.4 CenterY=-43.5 CenterZ=0 NormalX=0 NormalY=0 NormalZ=1 AngleXU=0 Radius=2.65 StartAngle=4.71239 EndAngle=6.28319
    g5: LineSegment StartX=31.4 StartY=-46.15 StartZ=0 EndX=2.4 EndY=-46.15 EndZ=0
    g6: ArcOfCircle CenterX=2.4 CenterY=-43.5 CenterZ=0 NormalX=0 NormalY=0 NormalZ=1 AngleXU=0 Radius=2.65 StartAngle=3.14159 EndAngle=4.71239
    g7: LineSegment StartX=-0.25 StartY=-43.5 StartZ=0 EndX=-0.25 EndY=-2.50001 EndZ=0
    g8: ArcOfCircle CenterX=2.4 CenterY=-2.5 CenterZ=0 NormalX=0 NormalY=0 NormalZ=1 AngleXU=0 Radius=2 StartAngle=1.5708 EndAngle=3.14159
    g9: ArcOfCircle CenterX=31.4 CenterY=-2.5 CenterZ=0 NormalX=0 NormalY=0 NormalZ=1 AngleXU=0 Radius=2 StartAngle=0 EndAngle=1.5708
    g10: ArcOfCircle CenterX=31.4 CenterY=-43.5 CenterZ=0 NormalX=0 NormalY=0 NormalZ=1 AngleXU=0 Radius=2 StartAngle=4.71239 EndAngle=6.28319
    g11: ArcOfCircle CenterX=2.4 CenterY=-43.5 CenterZ=0 NormalX=0 NormalY=0 NormalZ=1 AngleXU=0 Radius=2 StartAngle=3.14159 EndAngle=4.71239
    g12: LineSegment StartX=2.4 StartY=-0.5 StartZ=0 EndX=31.4 EndY=-0.5 EndZ=0
    g13: LineSegment StartX=33.4 StartY=-2.5 StartZ=0 EndX=33.4 EndY=-43.5 EndZ=0
    g14: LineSegment StartX=31.4 StartY=-45.5 StartZ=0 EndX=2.4 EndY=-45.5 EndZ=0
    g15: LineSegment StartX=0.4 StartY=-43.5 StartZ=0 EndX=0.4 EndY=-2.5 EndZ=0
  constraints (27):
    c: Vertical(g3)
    c: Horizontal(g5)
    c: Coincident(g7,g0)
    c: Vertical(g7)
    c: Tangent(g1,g0) = 1.5708
    c: Tangent(g2,g1) = 1.5708
    c: Tangent(g3,g2) = 1.5708
    c: Tangent(g4,g3) = 1.5708
    c: Tangent(g5,g4) = 1.5708
    c: Tangent(g6,g5) = 1.5708
    c: Tangent(g7,g6) = 1.5708
    c: Coincident(g8,g0)
    c: Coincident(g9,g2)
    c: Coincident(g10,g4)
    c: Coincident(g11,g6)
    c: Coincident(g12,g8)
    c: Coincident(g12,g9)
    c: Horizontal(g12)
    c: Vertical(g13)
    c: Horizontal(g14)
    c: Vertical(g15)
    c: Tangent(g15,g8) = 1.5708
    c: Tangent(g15,g11) = 1.5708
    c: Tangent(g14,g11) = 1.5708
    c: Tangent(g14,g10) = 1.5708
    c: Tangent(g13,g10) = 1.5708
    c: Tangent(g13,g9) = 1.5708
FEATURE [PartDesign::Pad] Pad013
  BaseFeature = -> Pocket006
  Direction = (0,4e-15,-1)
  Length = 1
  Length2 = 10
  Placement = pos=(0,-2.9e-15,6.5) rot=(0,0,1;0rad)
  Profile = -> Sketch021
  ReferenceAxis = -> Sketch021 [N_Axis]
  Type = 0
FEATURE [Sketcher::SketchObject] Sketch022
  ExternalGeometry = -> [Pad013]
  FullyConstrained = true
  MapMode = 5
  Placement = pos=(0,-5.1e-15,9.5) rot=(1,0,0;3.14159rad)
  Support = -> [Pad013]
  sketch-geometry (9):
    g0: GeomPoint X=16.9 Y=-23 Z=0
    g1: LineSegment StartX=2.9 StartY=-10 StartZ=0 EndX=30.9 EndY=-10 EndZ=0
    g2: LineSegment StartX=30.9 StartY=-10 StartZ=0 EndX=30.9 EndY=-13 EndZ=0
    g3: LineSegment StartX=30.9 StartY=-13 StartZ=0 EndX=2.9 EndY=-13 EndZ=0
    g4: LineSegment StartX=2.9 StartY=-13 StartZ=0 EndX=2.9 EndY=-10 EndZ=0
    g5: LineSegment StartX=2.9 StartY=-33 StartZ=0 EndX=30.9 EndY=-33 EndZ=0
    g6: LineSegment StartX=30.9 StartY=-33 StartZ=0 EndX=30.9 EndY=-36 EndZ=0
    g7: LineSegment StartX=30.9 StartY=-36 StartZ=0 EndX=2.9 EndY=-36 EndZ=0
    g8: LineSegment StartX=2.9 StartY=-36 StartZ=0 EndX=2.9 EndY=-33 EndZ=0
  constraints (23):
    c: Coincident(g1,g2)
    c: Coincident(g2,g3)
    c: Coincident(g3,g4)
    c: Coincident(g4,g1)
    c: Horizontal(g1)
    c: Horizontal(g3)
    c: Vertical(g2)
    c: Vertical(g4)
    c: Coincident(g5,g6)
    c: Coincident(g6,g7)
    c: Coincident(g7,g8)
    c: Coincident(g8,g5)
    c: Horizontal(g7)
    c: Vertical(g6)
    c: Vertical(g8)
    c: DistanceX(g1,g1) = 28
    c: DistanceY(g2,g2) = 3
    c: Equal(g2,g6)
    c: Symmetric(g5,g2,g0)
    c: Symmetric(g5,g3,g0)
    c: DistanceX(g5,g3) = 0
    c: DistanceY(g5,g2) = 20
    c: Symmetric(g-3,g-4,g0)
FEATURE [PartDesign::Pad] Pad014
  BaseFeature = -> Pad013
  Direction = (0,1.5e-15,-1)
  Length = 3
  Length2 = 10
  Placement = pos=(0,-2.9e-15,6.5) rot=(0,0,1;0rad)
  Profile = -> Sketch022
  ReferenceAxis = -> Sketch022 [N_Axis]
  Type = 0
FEATURE [Sketcher::SketchObject] Sketch023
  ExternalGeometry = -> [Pad014]
  FullyConstrained = true
  MapMode = 5
  Placement = pos=(0,-5.1e-15,9.5) rot=(1,0,0;3.14159rad)
  Support = -> [Pad014]
  sketch-geometry (12):
    g0: ArcOfCircle CenterX=2.4 CenterY=-43.5 CenterZ=0 NormalX=0 NormalY=0 NormalZ=1 AngleXU=0 Radius=2 StartAngle=3.14159 EndAngle=4.71239
    g1: ArcOfCircle CenterX=31.4 CenterY=-43.5 CenterZ=0 NormalX=0 NormalY=0 NormalZ=1 AngleXU=0 Radius=2 StartAngle=4.71239 EndAngle=6.28319
    g2: ArcOfCircle CenterX=2.4 CenterY=-2.5 CenterZ=0 NormalX=0 NormalY=0 NormalZ=1 AngleXU=0 Radius=2 StartAngle=1.5708 EndAngle=3.14159
    g3: ArcOfCircle CenterX=31.4 CenterY=-2.5 CenterZ=0 NormalX=0 NormalY=0 NormalZ=1 AngleXU=0 Radius=2 StartAngle=0 EndAngle=1.5708
    g4: LineSegment StartX=2.4 StartY=-0.5 StartZ=0 EndX=31.4 EndY=-0.5 EndZ=0
    g5: LineSegment StartX=2.4 StartY=-45.5 StartZ=0 EndX=31.4 EndY=-45.5 EndZ=0
    g6: LineSegment StartX=0.4 StartY=-43.5 StartZ=0 EndX=0.4 EndY=-39.7 EndZ=0
    g7: LineSegment StartX=0.4 StartY=-39.7 StartZ=0 EndX=33.4 EndY=-39.7 EndZ=0
    g8: LineSegment StartX=33.4 StartY=-39.7 StartZ=0 EndX=33.4 EndY=-43.5 EndZ=0
    g9: LineSegment StartX=0.4 StartY=-2.5 StartZ=0 EndX=0.4 EndY=-6.3 EndZ=0
    g10: LineSegment StartX=0.4 StartY=-6.3 StartZ=0 EndX=33.4 EndY=-6.3 EndZ=0
    g11: LineSegment StartX=33.4 StartY=-6.3 StartZ=0 EndX=33.4 EndY=-2.5 EndZ=0
  constraints (32):
    c: Coincident(g0,g-6)
    c: Coincident(g0,g-6)
    c: Coincident(g0,g-7)
    c: Coincident(g1,g-8)
    c: Coincident(g1,g-8)
    c: Coincident(g1,g-8)
    c: Coincident(g2,g-5)
    c: Coincident(g2,g-5)
    c: Coincident(g2,g-5)
    c: Coincident(g3,g-3)
    c: Coincident(g3,g-4)
    c: Coincident(g3,g-3)
    c: Coincident(g4,g2)
    c: Coincident(g4,g3)
    c: Coincident(g5,g0)
    c: Coincident(g5,g1)
    c: Coincident(g6,g0)
    c: Vertical(g6)
    c: Coincident(g7,g6)
    c: Horizontal(g7)
    c: Coincident(g8,g7)
    c: Coincident(g8,g1)
    c: Vertical(g8)
    c: DistanceY(g8,g8) = 3.8
    c: Coincident(g9,g2)
    c: Vertical(g9)
    c: Coincident(g10,g9)
    c: Horizontal(g10)
    c: Coincident(g11,g10)
    c: Coincident(g11,g3)
    c: Vertical(g11)
    c: Equal(g11,g8)
FEATURE [PartDesign::Pad] Pad015
  BaseFeature = -> Pad014
  Direction = (0,1.8e-15,-1)
  Length = 4
  Length2 = 10
  Placement = pos=(0,-2.9e-15,6.5) rot=(0,0,1;0rad)
  Profile = -> Sketch023
  ReferenceAxis = -> Sketch023 [N_Axis]
  Type = 0
FEATURE [Sketcher::SketchObject] Sketch024
  ExternalGeometry = -> [ShapeBinder001]
  FullyConstrained = true
  MapMode = 5
  Placement = pos=(0,-1.1e-15,5.5) rot=(1,0,0;3.14159rad)
  Support = -> [Pad015]
  sketch-geometry (6):
    g0: Circle CenterX=5.9 CenterY=-42.96 CenterZ=0 NormalX=0 NormalY=0 NormalZ=1 AngleXU=0 Radius=1
    g1: Circle CenterX=27.9 CenterY=-42.96 CenterZ=0 NormalX=0 NormalY=0 NormalZ=1 AngleXU=0 Radius=1
    g2: Circle CenterX=5.9 CenterY=-3 CenterZ=0 NormalX=0 NormalY=0 NormalZ=1 AngleXU=0 Radius=1
    g3: Circle CenterX=27.9 CenterY=-3 CenterZ=0 NormalX=0 NormalY=0 NormalZ=1 AngleXU=0 Radius=1
    g4: LineSegment StartX=3.9 StartY=-42.96 StartZ=0 EndX=29.9 EndY=-42.96 EndZ=0
    g5: LineSegment StartX=3.9 StartY=-3 StartZ=0 EndX=29.9 EndY=-3 EndZ=0
  constraints (16):
    c: PointOnObject(g3,g5)
    c: PointOnObject(g2,g5)
    c: PointOnObject(g0,g4)
    c: PointOnObject(g1,g4)
    c: Diameter(g0) = 2
    c: Equal(g1,g0)
    c: Equal(g0,g2)
    c: Equal(g2,g3)
    c: DistanceX(g5,g2) = 2
    c: DistanceX(g3,g5) = 2
    c: DistanceX(g4,g0) = 2
    c: DistanceX(g1,g4) = 2
    c: Coincident(g5,g-3)
    c: Coincident(g5,g-4)
    c: Coincident(g4,g-5)
    c: Coincident(g4,g-6)
FEATURE [PartDesign::Pocket] Pocket012
  BaseFeature = -> Pad015
  Direction = (0,-2.2e-15,1)
  Length = 5
  Length2 = 5
  Placement = pos=(0,-2.9e-15,6.5) rot=(0,0,1;0rad)
  Profile = -> Sketch024
  ReferenceAxis = -> Sketch024 [N_Axis]
  Type = 1
FEATURE [Sketcher::SketchObject] Sketch025
  ExternalGeometry = -> [Pocket012]
  FullyConstrained = true
  MapMode = 5
  Placement = pos=(0,-4.3e-15,10.5) rot=(0,0,1;0rad)
  Support = -> [Pocket012]
  sketch-geometry (4):
    g0: Circle CenterX=5.9 CenterY=42.96 CenterZ=0 NormalX=0 NormalY=0 NormalZ=1 AngleXU=0 Radius=2.125
    g1: Circle CenterX=27.9 CenterY=42.96 CenterZ=0 NormalX=0 NormalY=0 NormalZ=1 AngleXU=0 Radius=2.125
    g2: Circle CenterX=5.9 CenterY=3 CenterZ=0 NormalX=0 NormalY=0 NormalZ=1 AngleXU=0 Radius=2.125
    g3: Circle CenterX=27.9 CenterY=3 CenterZ=0 NormalX=0 NormalY=0 NormalZ=1 AngleXU=0 Radius=2.125
  constraints (8):
    c: Coincident(g0,g-3)
    c: Coincident(g1,g-4)
    c: Coincident(g2,g-5)
    c: Coincident(g3,g-6)
    c: Diameter(g0) = 4.25
    c: Equal(g0,g1)
    c: Equal(g1,g3)
    c: Equal(g3,g2)
FEATURE [PartDesign::Pocket] Pocket013
  BaseFeature = -> Pocket012
  Direction = (0,2.6e-15,-1)
  Length = 3
  Length2 = 5
  Placement = pos=(0,-2.9e-15,6.5) rot=(0,0,1;0rad)
  Profile = -> Sketch025
  ReferenceAxis = -> Sketch025 [N_Axis]
  Type = 0
FEATURE [PartDesign::Fillet] Fillet009
  Base = -> Pocket013 [Edge136,Edge132,Edge131,Edge134,Edge139,Edge142,Edge140,Edge144]
  BaseFeature = -> Pocket013
  Placement = pos=(0,-2.9e-15,6.5) rot=(0,0,1;0rad)
  Radius = 1
  SupportTransform = false
  UseAllEdges = false
FEATURE [PartDesign::Body] Body002  label="Case_Bottom"
  Group = -> [DatumPlane001,ReferenceFillet003,Sketch009,Pad004,Fillet004,Sketch010,Pocket006,ShapeBinder001,Sketch021,Pad013,Sketch022,Pad014,Sketch023,Pad015,Sketch024,Pocket012,Sketch025,Pocket013,Fillet009]
  Origin = -> Origin115
  Tip = -> Fillet009
FEATURE [PartDesign::Pad] Pad016
  BaseFeature = -> Pocket011
  Direction = (0,-1.8e-15,1)
  Length = 0.4
  Length2 = 10
  Placement = pos=(0,0,-1.5) rot=(1,0,0;3.14159rad)
  Profile = -> Pocket011 [Face66]
  Type = 0
FEATURE [PartDesign::Pad] Pad018
  BaseFeature = -> Pad016
  Direction = (0,-1.4e-15,1)
  Length = 0.5
  Length2 = 10
  Placement = pos=(0,0,-1.5) rot=(1,0,0;3.14159rad)
  Profile = -> Pad016 [Face169,Face173,Face177,Face180,Face184,Face188]
  Type = 0
FEATURE [Part::Part2DObjectPython] ShapeString  # Draft 2D object (typed FeaturePython)
  FontFile = <userpath>/Téléchargements/ubuntu/Ubuntu-B.ttf
  MakeFace = true
  Placement = pos=(28.3629,3.34221,-2.5) rot=(0,1,0;3.14159rad)
  Size = 2.5
  String = Watchy
  Tracking = 0
FEATURE [Part::Extrusion] Extrude  label="Watchy"
  Base = -> ShapeString
  Dir = (0,0,-1)
  DirMode = 2
  FaceMakerClass = Part::FaceMakerBullseye
  LengthFwd = 0.5
  LengthRev = 0
  Placement = pos=(0.184744,0.772381,0.5) rot=(0,0,1;0rad)
  Solid = false
  Symmetric = false
FEATURE [PartDesign::ShapeBinder] ReferencePart__Feature055
  Support = -> [Part__Feature055]
  TraceSupport = false
FEATURE [PartDesign::Plane] DatumPlane002
  Length = 70.0989
  MapMode = 5
  Placement = pos=(0,0,1.6) rot=(0,0,1;0rad)
  ResizeMode = 0
  Support = -> [ReferencePart__Feature055]
  Width = 83.1771
FEATURE [Sketcher::SketchObject] Sketch026
  ExternalGeometry = -> [ReferencePart__Feature055]
  FullyConstrained = true
  MapMode = 5
  Placement = pos=(0,0,1.6) rot=(0,0,1;0rad)
  Support = -> [DatumPlane002]
  sketch-geometry (8):
    g0: ArcOfCircle CenterX=3.9 CenterY=42.96 CenterZ=0 NormalX=0 NormalY=0 NormalZ=1 AngleXU=0 Radius=1 StartAngle=1.5708 EndAngle=4.71239
    g1: ArcOfCircle CenterX=29.9 CenterY=42.96 CenterZ=0 NormalX=0 NormalY=0 NormalZ=1 AngleXU=0 Radius=1 StartAngle=4.71239 EndAngle=7.85398
    g2: LineSegment StartX=3.9 StartY=43.96 StartZ=0 EndX=29.9 EndY=43.96 EndZ=0
    g3: LineSegment StartX=29.9 StartY=41.96 StartZ=0 EndX=3.9 EndY=41.96 EndZ=0
    g4: ArcOfCircle CenterX=3.9 CenterY=42.96 CenterZ=0 NormalX=0 NormalY=0 NormalZ=1 AngleXU=0 Radius=2.5 StartAngle=1.5708 EndAngle=4.71239
    g5: ArcOfCircle CenterX=29.9 CenterY=42.96 CenterZ=0 NormalX=0 NormalY=0 NormalZ=1 AngleXU=0 Radius=2.5 StartAngle=4.71239 EndAngle=7.85398
    g6: LineSegment StartX=3.9 StartY=45.46 StartZ=0 EndX=29.9 EndY=45.46 EndZ=0
    g7: LineSegment StartX=3.9 StartY=40.46 StartZ=0 EndX=29.9 EndY=40.46 EndZ=0
  constraints (19):
    c: Coincident(g0,g-4)
    c: Coincident(g0,g-4)
    c: Coincident(g0,g-5)
    c: Coincident(g1,g-6)
    c: Coincident(g1,g-6)
    c: Coincident(g1,g-6)
    c: Coincident(g2,g0)
    c: Coincident(g2,g1)
    c: Coincident(g3,g1)
    c: Coincident(g3,g0)
    c: Coincident(g5,g1)
    c: Horizontal(g6)
    c: Horizontal(g7)
    c: DistanceY(g0,g4) = 1.5
    c: Tangent(g6,g4) = 1.5708
    c: Tangent(g6,g5) = 1.5708
    c: Tangent(g7,g5) = -1.5708
    c: Tangent(g7,g4) = -1.5708
    c: Coincident(g0,g4)
FEATURE [PartDesign::Pad] Pad019
  Direction = (0,0,1)
  Length = 3.5
  Length2 = 10
  Placement = pos=(0,0,1.6) rot=(0,0,1;0rad)
  Profile = -> Sketch026
  ReferenceAxis = -> Sketch026 [N_Axis]
  Type = 0
FEATURE [PartDesign::Body] Body003  label="Bride"
  Group = -> [DatumPlane002,ReferencePart__Feature055,Sketch026,Pad019]
  Origin = -> Origin116
  Tip = -> Pad019
FEATURE [PartDesign::FeatureBase] Clone
  BaseFeature = -> Body003
FEATURE [PartDesign::Body] Body004  label="Bride2"
  BaseFeature = -> Body003
  Group = -> [Clone]
  Origin = -> Origin117
  Placement = pos=(0,-40,0) rot=(0,0,1;0rad)
  Tip = -> Clone
FEATURE [Mesh::Feature] Micro_USB_Cover
  Placement = pos=(36.4,26.7,5) rot=(0.707107,-0.707107,0;3.14159rad)
FEATURE [Part::Feature] Micro_USB_Cover001
  shape: bbox 6 x 8.5 x 3.5 mm, 1068 faces, 0 solids (baked)
FEATURE [Sketcher::SketchObject] Sketch027
  FullyConstrained = true
  MapMode = 5
  Placement = pos=(0,0,0) rot=(0.57735,0.57735,0.57735;2.0944rad)
  Support = -> [YZ_Plane118]
  sketch-geometry (4):
    g0: LineSegment StartX=17.7 StartY=5.55 StartZ=0 EndX=27.2 EndY=5.55 EndZ=0
    g1: LineSegment StartX=27.2 StartY=5.55 StartZ=0 EndX=27.2 EndY=0.95 EndZ=0
    g2: LineSegment StartX=27.2 StartY=0.95 StartZ=0 EndX=17.7 EndY=0.95 EndZ=0
    g3: LineSegment StartX=17.7 StartY=0.95 StartZ=0 EndX=17.7 EndY=5.55 EndZ=0
  constraints (12):
    c: Coincident(g0,g1)
    c: Coincident(g1,g2)
    c: Coincident(g2,g3)
    c: Coincident(g3,g0)
    c: Horizontal(g0)
    c: Horizontal(g2)
    c: Vertical(g1)
    c: Vertical(g3)
    c: DistanceX(g0,g0) = 9.5
    c: DistanceY(g1,g1) = 4.6
    c: DistanceY(g-1,g2) = 0.95
    c: DistanceX(g-1,g2) = 17.7
FEATURE [PartDesign::Pad] Pad020
  Direction = (1,-2e-16,3e-16)
  Length = 2
  Length2 = 10
  Placement = pos=(0,0,0) rot=(0.57735,0.57735,0.57735;2.0944rad)
  Profile = -> Sketch027
  ReferenceAxis = -> Sketch027 [N_Axis]
  Type = 0
FEATURE [Part::Feature] Micro_USB_Cover001_solid  label="Micro_USB_Cover001 (Solid)"
  Placement = pos=(0.5,0,0) rot=(0,0,1;0rad)
  shape: bbox 6 x 8.5 x 3.5 mm, 1068 faces (baked)
FEATURE [PartDesign::ShapeBinder] ShapeBinder002
  Support = -> [Micro_USB_Cover001_solid]
  TraceSupport = false
FEATURE [PartDesign::Fillet] Fillet010
  Base = -> Pad020 [Edge1,Edge8,Edge5,Edge2,Edge4,Edge7,Edge10,Edge12]
  BaseFeature = -> Pad020
  Placement = pos=(0,0,0) rot=(0.57735,0.57735,0.57735;2.0944rad)
  Radius = 1
  SupportTransform = false
  UseAllEdges = false
FEATURE [PartDesign::Body] Body005
  Group = -> [Sketch027,Pad020,ShapeBinder002,Fillet010]
  Origin = -> Origin118
  Placement = pos=(35.4,0,0) rot=(0,0,1;0rad)
  Tip = -> Fillet010
FEATURE [Part::Fuse] Fusion  label="USB_Cap"
  Base = -> Body005
  Tool = -> Micro_USB_Cover001_solid
FEATURE [PartDesign::ShapeBinder] ShapeBinder003
  Placement = pos=(0,0,-2.5) rot=(1,0,0;3.14159rad)
  Support = -> [Sketch002]
  TraceSupport = false
FEATURE [Sketcher::SketchObject] Sketch028
  ExternalGeometry = -> [ShapeBinder003]
  FullyConstrained = true
  MapMode = 5
  Placement = pos=(0,0,-1.5) rot=(1,0,0;3.14159rad)
  Support = -> [Pocket]
  sketch-geometry (4):
    g0: LineSegment StartX=3 StartY=-12.3 StartZ=0 EndX=31 EndY=-12.3 EndZ=0
    g1: LineSegment StartX=31 StartY=-39.3 StartZ=0 EndX=31 EndY=-12.3 EndZ=0
    g2: LineSegment StartX=31 StartY=-39.3 StartZ=0 EndX=3 EndY=-39.3 EndZ=0
    g3: LineSegment StartX=3 StartY=-12.3 StartZ=0 EndX=3 EndY=-39.3 EndZ=0
  constraints (8):
    c: Coincident(g0,g-3)
    c: Coincident(g0,g-4)
    c: Coincident(g1,g-5)
    c: Coincident(g1,g0)
    c: Coincident(g2,g1)
    c: Coincident(g2,g-5)
    c: Coincident(g3,g0)
    c: Coincident(g3,g2)
FEATURE [PartDesign::Pad] Pad021
  BaseFeature = -> Pocket
  Direction = (0,0,-1)
  Length = 0.8
  Length2 = 10
  Profile = -> Sketch028
  ReferenceAxis = -> Sketch028 [N_Axis]
  Type = 0
FEATURE [PartDesign::Body] Body  label="Vitre"
  Group = -> [Sketch,Pad,Fillet,Pocket,ShapeBinder003,Sketch028,Pad021]
  Origin = -> Origin056
  Tip = -> Pad021
FEATURE [PartDesign::Pocket] Pocket014
  BaseFeature = -> Pad018
  Direction = (0,2.1e-15,-1)
  Length = 0.73
  Length2 = 5
  Placement = pos=(0,0,-1.5) rot=(1,0,0;3.14159rad)
  Profile = -> Pad018 [Face67]
  Type = 0
FEATURE [PartDesign::Pocket] Pocket015
  BaseFeature = -> Pocket014
  Direction = (0,2e-15,-1)
  Length = 0.33
  Length2 = 5
  Placement = pos=(0,0,-1.5) rot=(1,0,0;3.14159rad)
  Profile = -> Pocket014 [Face113,Face111,Face117,Face116]
  Type = 0
FEATURE [Sketcher::SketchObject] Sketch029
  ExternalGeometry = -> [Pocket015]
  FullyConstrained = true
  MapMode = 5
  Placement = pos=(0,-3e-16,0.65) rot=(0,0,1;0rad)
  Support = -> [Pocket015]
  sketch-geometry (4):
    g0: LineSegment StartX=34.7 StartY=26.9 StartZ=0 EndX=35.1 EndY=26.9 EndZ=0
    g1: LineSegment StartX=35.1 StartY=26.9 StartZ=0 EndX=35.1 EndY=18 EndZ=0
    g2: LineSegment StartX=35.1 StartY=18 StartZ=0 EndX=34.7 EndY=18 EndZ=0
    g3: LineSegment StartX=34.7 StartY=18 StartZ=0 EndX=34.7 EndY=26.9 EndZ=0
  constraints (12):
    c: Coincident(g0,g1)
    c: Coincident(g1,g2)
    c: Coincident(g2,g3)
    c: Coincident(g3,g0)
    c: Horizontal(g0)
    c: Horizontal(g2)
    c: Vertical(g1)
    c: Vertical(g3)
    c: DistanceX(g0,g0) = 0.4
    c: DistanceY(g-4,g0) = 1
    c: DistanceY(g1,g-4) = 1
    c: DistanceX(g-3,g0) = 0.3
FEATURE [PartDesign::Pad] Pad022
  BaseFeature = -> Pocket015
  Direction = (0,-2.2e-15,1)
  Length = 5
  Length2 = 10
  Placement = pos=(0,0,-1.5) rot=(1,0,0;3.14159rad)
  Profile = -> Sketch029
  ReferenceAxis = -> Sketch029 [N_Axis]
  Type = 0
FEATURE [PartDesign::Body] Body001  label="Case_Top"
  Group = -> [DatumPlane,ReferencePocket,Sketch001,Pad001,Sketch002,Pocket001,Sketch003,Pocket002,Sketch004,Pocket003,Sketch005,Pocket004,Sketch006,Pocket005,Sketch007,Pad002,Sketch008,Pad003,Fillet001,Fillet002,Fillet003,Sketch011,Pad005,Pad006,Pad007,Fillet005,Sketch012,Pad008,Pad009,Fillet006,Fillet007,Sketch014,Pocket007,Pad010,Sketch015,Pocket008,Sketch016,ShapeBinder,Pad011,Sketch020,Pocket011,Pad016,+5 more]
  Origin = -> Origin057
  Tip = -> Pad022
FEATURE [Part::Cut] Cut  label="Case_Top_Watchy"
  Base = -> Body001
  Tool = -> Extrude
FEATURE [PartDesign::ShapeBinder] ShapeBinder004
  Placement = pos=(0,0,-0.8) rot=(0,0,1;0rad)
  Support = -> [Pad021]
  TraceSupport = false
FEATURE [PartDesign::ShapeBinder] ShapeBinder005
  Support = -> [Pad021]
  TraceSupport = false
FEATURE [Part::Feature] Part__Feature056  label="SOLID010"
  shape: bbox 4 x 4 x 1.1 mm, 158 faces (baked)
FEATURE [App::Part] QFN_24_1EP_4x4mm_P0_5mm_EP2_7x2_7mm001  label="QFN-24-1EP_4x4mm_P0.5mm_EP2.7x2.7mm001"
  Group = -> [Part__Feature056]
  Origin = -> Origin135
  Placement = pos=(25.76,24.38,1.05) rot=(0,0,1;0rad)
FEATURE [Part::Feature] Part__Feature057  label="SOLID011"
  shape: bbox 3.8 x 1.6 x 1.25 mm, 67 faces (baked)
FEATURE [App::Part] D_SOD_123004  label="D_SOD-127"
  Group = -> [Part__Feature057]
  Origin = -> Origin136
  Placement = pos=(5.85,15.82,1.05) rot=(0,0,-1;1.5708rad)
FEATURE [Part::Feature] Part__Feature058  label="SOLID012"
  shape: bbox 7 x 7 x 0.77 mm, 302 faces (baked)
FEATURE [App::Part] QFN_48_1EP_7x7mm_P0_5mm_EP5_15x5_15mm001  label="QFN-48-1EP_7x7mm_P0.5mm_EP5.15x5.15mm001"
  Group = -> [Part__Feature058]
  Origin = -> Origin137
  Placement = pos=(17.7737,29.6588,1.05) rot=(0,0,-1;1.5708rad)
FEATURE [Part::Feature] Part__Feature059  label="SOLID013"
  shape: bbox 6.652 x 4.89 x 2.436 mm, 452 faces (baked)
FEATURE [App::Part] Button004
  Group = -> [Part__Feature059]
  Origin = -> Origin138
  Placement = pos=(2.48,8.73,1.05) rot=(0,0,-1;1.5708rad)
FEATURE [Part::Feature] Part__Feature060  label="SOLID014"
  shape: bbox 6.652 x 4.89 x 2.436 mm, 452 faces (baked)
FEATURE [App::Part] Button005
  Group = -> [Part__Feature060]
  Origin = -> Origin139
  Placement = pos=(31.32,10.53,1.05) rot=(0,0,1;1.5708rad)
FEATURE [Part::Feature] Part__Feature061  label="SOLID015"
  shape: bbox 3.8 x 1.6 x 1.25 mm, 67 faces (baked)
FEATURE [App::Part] D_SOD_123005  label="D_SOD-128"
  Group = -> [Part__Feature061]
  Origin = -> Origin140
  Placement = pos=(3.55,15.82,1.05) rot=(0,0,-1;1.5708rad)
FEATURE [Part::Feature] Part__Feature062  label="SOLID016"
  shape: bbox 7.65 x 5.2 x 3.4 mm, 136 faces (baked)
FEATURE [App::Part] Molex_PicoBlade_53261_0271_1x02_1MP_P1_25mm_Horizontal001  label="Molex_PicoBlade_53261-0271_1x02-1MP_P1.25mm_Horizontal001"
  Group = -> [Part__Feature062]
  Origin = -> Origin141
  Placement = pos=(28.63,31.39,1.05) rot=(0,0,-1;1.5708rad)
FEATURE [Part::Feature] Part__Feature063  label="SOLID017"
  shape: bbox 6.652 x 4.89 x 2.436 mm, 452 faces (baked)
FEATURE [App::Part] Button006
  Group = -> [Part__Feature063]
  Origin = -> Origin142
  Placement = pos=(31.32,37.23,1.05) rot=(0,0,1;1.5708rad)
FEATURE [Part::Feature] Part__Feature064  label="SOLID018"
  shape: bbox 6.652 x 4.89 x 2.436 mm, 452 faces (baked)
FEATURE [App::Part] Button007
  Group = -> [Part__Feature064]
  Origin = -> Origin143
  Placement = pos=(2.48,35.43,1.05) rot=(0,0,-1;1.5708rad)
FEATURE [Part::Feature] Part__Feature065  label="COMPOUND001"
  shape: bbox 16.31 x 5.857 x 2.117 mm, 1280 faces, 17 solids (baked)
FEATURE [App::Part] FPC_24001  label="FPC-025"
  Group = -> [Part__Feature065]
  Origin = -> Origin144
  Placement = pos=(11.025,19.09,1.05) rot=(0,0,1;0rad)
FEATURE [Part::Feature] Part__Feature066  label="COMPOUND002"
  shape: bbox 13 x 10 x 2.5 mm, 15 faces, 3 solids (baked)
FEATURE [App::Part] PagerMotor001
  Group = -> [Part__Feature066]
  Origin = -> Origin145
  Placement = pos=(5.45,22.955,4.55) rot=(0.819152,-0.573576,0;3.14159rad)
FEATURE [Part::Feature] Part__Feature067  label="SOLID019"
  shape: bbox 7.981 x 5.421 x 2.94 mm, 484 faces (baked)
FEATURE [App::Part] USB_Micro_B_Molex_47346_0001001  label="USB_Micro-B_Molex_47346-0002"
  Group = -> [Part__Feature067]
  Origin = -> Origin146
  Placement = pos=(31.38,22.43,1.05) rot=(0,0,1;1.5708rad)
FEATURE [Part::Feature] Part__Feature068  label="SOLID020"
  shape: bbox 3 x 2.9 x 0.6 mm, 74 faces (baked)
FEATURE [App::Part] DFN_10_1EP_3x3mm_P0_5mm_EP1_75x2_7mm  label="DFN-10-1EP_3x3mm_P0.5mm_EP1.75x2.7mm"
  Group = -> [Part__Feature068]
  Origin = -> Origin147
  Placement = pos=(11.76,32.64,1.05) rot=(0,0,-1;1.5708rad)
FEATURE [Part::Feature] Part__Feature069  label="COMPOUND003"
  shape: bbox 37.16 x 32.08 x 2.7 mm, 85 faces, 2 solids (baked)
FEATURE [App::Part] Display001
  Group = -> [Part__Feature069]
  Origin = -> Origin148
  Placement = pos=(16.89,23.15,-0.05) rot=(0.707107,0.707107,0;3.14159rad)
FEATURE [Part::Feature] Part__Feature070  label="Watchy PCB"
  shape: bbox 33.8 x 37.96 x 1 mm, 34 faces (baked)
FEATURE [PartDesign::ShapeBinder] ShapeBinder006
  Support = -> [Part__Feature070]
  TraceSupport = false
FEATURE [Sketcher::SketchObject] Sketch030
  ExternalGeometry = -> [ShapeBinder005,ShapeBinder006]
  FullyConstrained = true
  MapMode = 5
  Placement = pos=(0,0,-2.3) rot=(1,0,0;3.14159rad)
  Support = -> [ShapeBinder004]
  sketch-geometry (4):
    g0: LineSegment StartX=-1.8 StartY=-2.2 StartZ=0 EndX=35.6 EndY=-2.2 EndZ=0
    g1: LineSegment StartX=35.6 StartY=-2.2 StartZ=0 EndX=35.6 EndY=-43.76 EndZ=0
    g2: LineSegment StartX=35.6 StartY=-43.76 StartZ=0 EndX=-1.8 EndY=-43.76 EndZ=0
    g3: LineSegment StartX=-1.8 StartY=-43.76 StartZ=0 EndX=-1.8 EndY=-2.2 EndZ=0
  constraints (12):
    c: Coincident(g0,g1)
    c: Coincident(g1,g2)
    c: Coincident(g2,g3)
    c: Coincident(g3,g0)
    c: Horizontal(g0)
    c: Horizontal(g2)
    c: Vertical(g1)
    c: Vertical(g3)
    c: DistanceX(g0,g-8) = 1.8
    c: DistanceX(g-7,g1) = 1.8
    c: DistanceY(g1,g-7) = 1.8
    c: DistanceY(g-8,g0) = 1.8
FEATURE [PartDesign::Pad] Pad023
  Direction = (0,0,-1)
  Length = 9
  Length2 = 10
  Placement = pos=(0,0,-0.8) rot=(0,0,1;0rad)
  Profile = -> Sketch030
  ReferenceAxis = -> Sketch030 [N_Axis]
  Reversed = true
  Type = 0
FEATURE [Sketcher::SketchObject] Sketch031
  ExternalGeometry = -> [ShapeBinder005]
  FullyConstrained = true
  MapMode = 5
  Placement = pos=(0,0,-2.3) rot=(1,0,0;3.14159rad)
  Support = -> [Pad023]
  sketch-geometry (4):
    g0: LineSegment StartX=2.8 StartY=-12.1 StartZ=0 EndX=31.2 EndY=-12.1 EndZ=0
    g1: LineSegment StartX=31.2 StartY=-12.1 StartZ=0 EndX=31.2 EndY=-39.5 EndZ=0
    g2: LineSegment StartX=31.2 StartY=-39.5 StartZ=0 EndX=2.8 EndY=-39.5 EndZ=0
    g3: LineSegment StartX=2.8 StartY=-39.5 StartZ=0 EndX=2.8 EndY=-12.1 EndZ=0
  constraints (12):
    c: Coincident(g0,g1)
    c: Coincident(g1,g2)
    c: Coincident(g2,g3)
    c: Coincident(g3,g0)
    c: Horizontal(g0)
    c: Horizontal(g2)
    c: Vertical(g1)
    c: Vertical(g3)
    c: DistanceY(g-3,g0) = 0.2
    c: DistanceY(g1,g-4) = 0.2
    c: DistanceX(g2,g-4) = 0.2
    c: DistanceX(g-3,g0) = 0.2
FEATURE [PartDesign::Pocket] Pocket016
  BaseFeature = -> Pad023
  Direction = (0,0,1)
  Length = 0.8
  Length2 = 5
  Placement = pos=(0,0,-0.8) rot=(0,0,1;0rad)
  Profile = -> Sketch031
  ReferenceAxis = -> Sketch031 [N_Axis]
  Type = 0
FEATURE [Sketcher::SketchObject] Sketch032
  ExternalGeometry = -> [ShapeBinder006]
  FullyConstrained = true
  MapMode = 5
  Placement = pos=(0,0,6.7) rot=(0,0,1;0rad)
  Support = -> [Pocket016]
  sketch-geometry (4):
    g0: LineSegment StartX=-0.2 StartY=42.16 StartZ=0 EndX=34 EndY=42.16 EndZ=0
    g1: LineSegment StartX=34 StartY=42.16 StartZ=0 EndX=34 EndY=3.8 EndZ=0
    g2: LineSegment StartX=34 StartY=3.8 StartZ=0 EndX=-0.2 EndY=3.8 EndZ=0
    g3: LineSegment StartX=-0.2 StartY=3.8 StartZ=0 EndX=-0.2 EndY=42.16 EndZ=0
  constraints (12):
    c: Coincident(g0,g1)
    c: Coincident(g1,g2)
    c: Coincident(g2,g3)
    c: Coincident(g3,g0)
    c: Horizontal(g0)
    c: Horizontal(g2)
    c: Vertical(g1)
    c: Vertical(g3)
    c: DistanceX(g0,g-4) = 0.2
    c: DistanceY(g-4,g0) = 0.2
    c: DistanceY(g1,g-3) = 0.2
    c: DistanceX(g-3,g1) = 0.2
FEATURE [PartDesign::Pocket] Pocket017
  BaseFeature = -> Pocket016
  Direction = (0,0,-1)
  Length = 8.2
  Length2 = 5
  Placement = pos=(0,0,-0.8) rot=(0,0,1;0rad)
  Profile = -> Sketch032
  ReferenceAxis = -> Sketch032 [N_Axis]
  Type = 0
FEATURE [Sketcher::SketchObject] Sketch033
  ExternalGeometry = -> [ShapeBinder006]
  FullyConstrained = true
  MapMode = 5
  Placement = pos=(0,0,6.7) rot=(0,0,1;0rad)
  Support = -> [Pocket017]
  sketch-geometry (20):
    g0: LineSegment StartX=33.8 StartY=10.93 StartZ=0 EndX=34.7 EndY=10.93 EndZ=0
    g1: LineSegment StartX=34.7 StartY=10.93 StartZ=0 EndX=34.7 EndY=8.33 EndZ=0
    g2: LineSegment StartX=34.7 StartY=8.33 StartZ=0 EndX=33.8 EndY=8.33 EndZ=0
    g3: LineSegment StartX=33.8 StartY=8.33 StartZ=0 EndX=33.8 EndY=10.93 EndZ=0
    g4: GeomPoint X=34.25 Y=9.63 Z=0
    g5: LineSegment StartX=33.8 StartY=37.63 StartZ=0 EndX=34.7 EndY=37.63 EndZ=0
    g6: LineSegment StartX=34.7 StartY=37.63 StartZ=0 EndX=34.7 EndY=35.03 EndZ=0
    g7: LineSegment StartX=34.7 StartY=35.03 StartZ=0 EndX=33.8 EndY=35.03 EndZ=0
    g8: LineSegment StartX=33.8 StartY=35.03 StartZ=0 EndX=33.8 EndY=37.63 EndZ=0
    g9: LineSegment StartX=-0.9 StartY=10.93 StartZ=0 EndX=-1e-12 EndY=10.93 EndZ=0
    g10: LineSegment StartX=-1e-12 StartY=10.93 StartZ=0 EndX=-1e-12 EndY=8.33 EndZ=0
    g11: LineSegment StartX=-1e-12 StartY=8.33 StartZ=0 EndX=-0.9 EndY=8.33 EndZ=0
    g12: LineSegment StartX=-0.9 StartY=8.33 StartZ=0 EndX=-0.9 EndY=10.93 EndZ=0
    g13: LineSegment StartX=-0.9 StartY=37.63 StartZ=0 EndX=9.9463e-12 EndY=37.63 EndZ=0
    g14: LineSegment StartX=9.9463e-12 StartY=37.63 StartZ=0 EndX=9.9463e-12 EndY=35.03 EndZ=0
    g15: LineSegment StartX=9.9463e-12 StartY=35.03 StartZ=0 EndX=-0.9 EndY=35.03 EndZ=0
    g16: LineSegment StartX=-0.9 StartY=35.03 StartZ=0 EndX=-0.9 EndY=37.63 EndZ=0
    g17: GeomPoint X=34.25 Y=36.33 Z=0
    g18: GeomPoint X=-0.45 Y=9.63 Z=0
    g19: GeomPoint X=-0.45 Y=36.33 Z=0
  constraints (52):
    c: Coincident(g0,g1)
    c: Coincident(g1,g2)
    c: Coincident(g2,g3)
    c: Coincident(g3,g0)
    c: Horizontal(g0)
    c: Horizontal(g2)
    c: Vertical(g1)
    c: Vertical(g3)
    c: DistanceX(g2,g2) = 0.9
    c: DistanceY(g1,g1) = 2.6
    c: Symmetric(g0,g2,g4)
    c: Coincident(g5,g6)
    c: Coincident(g6,g7)
    c: Coincident(g7,g8)
    c: Coincident(g8,g5)
    c: Horizontal(g5)
    c: Horizontal(g7)
    c: Vertical(g6)
    c: Vertical(g8)
    c: Coincident(g9,g10)
    c: Coincident(g10,g11)
    c: Coincident(g11,g12)
    c: Coincident(g12,g9)
    c: Horizontal(g9)
    c: Horizontal(g11)
    c: Vertical(g10)
    c: Vertical(g12)
    c: Coincident(g13,g14)
    c: Coincident(g14,g15)
    c: Coincident(g15,g16)
    c: Coincident(g16,g13)
    c: Horizontal(g13)
    c: Horizontal(g15)
    c: Vertical(g14)
    c: Vertical(g16)
    c: Equal(g5,g0)
    c: Equal(g9,g5)
    c: Equal(g13,g9)
    c: Equal(g6,g1)
    c: Equal(g10,g6)
    c: Equal(g10,g14)
    c: Symmetric(g5,g7,g17)
    c: Symmetric(g9,g11,g18)
    c: Symmetric(g13,g15,g19)
    c: DistanceY(g19,g-4) = 5.63
    c: DistanceY(g17,g-3) = 5.63
    c: DistanceY(g-3,g4) = 5.63
    c: DistanceY(g-4,g18) = 5.63
    c: PointOnObject(g10,g-4)
    c: PointOnObject(g14,g-4)
    c: PointOnObject(g7,g-3)
    c: PointOnObject(g2,g-3)
FEATURE [PartDesign::Pocket] Pocket018
  BaseFeature = -> Pocket017
  Direction = (0,0,-1)
  Length = 8
  Length2 = 5
  Placement = pos=(0,0,-0.8) rot=(0,0,1;0rad)
  Profile = -> Sketch033
  ReferenceAxis = -> Sketch033 [N_Axis]
  Type = 0
FEATURE [App::Part] Watchy_1  label="Watchy 1"
  Group = -> [QFN_24_1EP_4x4mm_P0_5mm_EP2_7x2_7mm001,D_SOD_123004,QFN_48_1EP_7x7mm_P0_5mm_EP5_15x5_15mm001,Button004,Button005,D_SOD_123005,Molex_PicoBlade_53261_0271_1x02_1MP_P1_25mm_Horizontal001,Button006,Button007,FPC_24001,PagerMotor001,USB_Micro_B_Molex_47346_0001001,DFN_10_1EP_3x3mm_P0_5mm_EP1_75x2_7mm,Display001,Part__Feature070]
  Origin = -> Origin149
FEATURE [Sketcher::SketchObject] Sketch034
  FullyConstrained = true
  MapMode = 5
  Placement = pos=(35.6,0,-0.8) rot=(0.57735,0.57735,0.57735;2.0944rad)
  Support = -> [Pocket018]
  sketch-geometry (4):
    g0: LineSegment StartX=18.18 StartY=4.79 StartZ=0 EndX=26.68 EndY=4.79 EndZ=0
    g1: LineSegment StartX=26.68 StartY=4.79 StartZ=0 EndX=26.68 EndY=1.39 EndZ=0
    g2: LineSegment StartX=26.68 StartY=1.39 StartZ=0 EndX=18.18 EndY=1.39 EndZ=0
    g3: LineSegment StartX=18.18 StartY=1.39 StartZ=0 EndX=18.18 EndY=4.79 EndZ=0
  constraints (12):
    c: Coincident(g0,g1)
    c: Coincident(g1,g2)
    c: Coincident(g2,g3)
    c: Coincident(g3,g0)
    c: Horizontal(g0)
    c: Horizontal(g2)
    c: Vertical(g1)
    c: Vertical(g3)
    c: DistanceX(g0,g0) = 8.5
    c: DistanceY(g1,g1) = 3.4
    c: DistanceX(g-1,g2) = 18.18
    c: DistanceY(g-1,g2) = 1.39
FEATURE [PartDesign::Pocket] Pocket019
  BaseFeature = -> Pocket018
  Direction = (-1,0,0)
  Length = 5
  Length2 = 5
  Placement = pos=(0,0,-0.8) rot=(0,0,1;0rad)
  Profile = -> Sketch034
  ReferenceAxis = -> Sketch034 [N_Axis]
  Type = 0
FEATURE [Sketcher::SketchObject] Sketch035
  ExternalGeometry = -> [ShapeBinder006]
  FullyConstrained = true
  MapMode = 5
  Placement = pos=(-1.8,0,-0.8) rot=(0.57735,-0.57735,-0.57735;2.0944rad)
  Support = -> [Pocket019]
  sketch-geometry (10):
    g0: LineSegment StartX=-6.625 StartY=4.05 StartZ=0 EndX=-12.625 EndY=4.05 EndZ=0
    g1: LineSegment StartX=-12.625 StartY=4.05 StartZ=0 EndX=-12.625 EndY=1.55 EndZ=0
    g2: LineSegment StartX=-12.625 StartY=1.55 StartZ=0 EndX=-6.625 EndY=1.55 EndZ=0
    g3: LineSegment StartX=-6.625 StartY=1.55 StartZ=0 EndX=-6.625 EndY=4.05 EndZ=0
    g4: GeomPoint X=-9.625 Y=2.8 Z=0
    g5: LineSegment StartX=-39.335 StartY=4.05 StartZ=0 EndX=-33.335 EndY=4.05 EndZ=0
    g6: LineSegment StartX=-33.335 StartY=4.05 StartZ=0 EndX=-33.335 EndY=1.55 EndZ=0
    g7: LineSegment StartX=-33.335 StartY=1.55 StartZ=0 EndX=-39.335 EndY=1.55 EndZ=0
    g8: LineSegment StartX=-39.335 StartY=1.55 StartZ=0 EndX=-39.335 EndY=4.05 EndZ=0
    g9: GeomPoint X=-36.335 Y=2.8 Z=0
  constraints (26):
    c: Coincident(g0,g1)
    c: Coincident(g1,g2)
    c: Coincident(g2,g3)
    c: Coincident(g3,g0)
    c: Horizontal(g0)
    c: Horizontal(g2)
    c: Vertical(g1)
    c: Vertical(g3)
    c: Symmetric(g0,g1,g4)
    c: DistanceX(g4,g-3) = 5.625
    c: DistanceY(g-3,g4) = 1
    c: DistanceX(g0,g0) = 6
    c: DistanceY(g3,g3) = 2.5
    c: Coincident(g5,g6)
    c: Coincident(g6,g7)
    c: Coincident(g7,g8)
    c: Coincident(g8,g5)
    c: Horizontal(g5)
    c: Horizontal(g7)
    c: Vertical(g6)
    c: Vertical(g8)
    c: Equal(g0,g5)
    c: Equal(g3,g6)
    c: Symmetric(g5,g6,g9)
    c: DistanceX(g-3,g9) = 5.625
    c: DistanceY(g-3,g9) = 1
FEATURE [PartDesign::Pad] Pad024
  BaseFeature = -> Pocket019
  Direction = (-1,0,0)
  Length = 1.25
  Length2 = 10
  Placement = pos=(0,0,-0.8) rot=(0,0,1;0rad)
  Profile = -> Sketch035
  ReferenceAxis = -> Sketch035 [N_Axis]
  Type = 0
FEATURE [Sketcher::SketchObject] Sketch036
  ExternalGeometry = -> [ShapeBinder006]
  FullyConstrained = true
  MapMode = 5
  Placement = pos=(35.6,0,-0.8) rot=(0.57735,0.57735,0.57735;2.0944rad)
  Support = -> [Pad024]
  sketch-geometry (10):
    g0: LineSegment StartX=6.625 StartY=4.05 StartZ=0 EndX=12.625 EndY=4.05 EndZ=0
    g1: LineSegment StartX=12.625 StartY=4.05 StartZ=0 EndX=12.625 EndY=1.55 EndZ=0
    g2: LineSegment StartX=12.625 StartY=1.55 StartZ=0 EndX=6.625 EndY=1.55 EndZ=0
    g3: LineSegment StartX=6.625 StartY=1.55 StartZ=0 EndX=6.625 EndY=4.05 EndZ=0
    g4: LineSegment StartX=33.335 StartY=4.05 StartZ=0 EndX=39.335 EndY=4.05 EndZ=0
    g5: LineSegment StartX=39.335 StartY=4.05 StartZ=0 EndX=39.335 EndY=1.55 EndZ=0
    g6: LineSegment StartX=39.335 StartY=1.55 StartZ=0 EndX=33.335 EndY=1.55 EndZ=0
    g7: LineSegment StartX=33.335 StartY=1.55 StartZ=0 EndX=33.335 EndY=4.05 EndZ=0
    g8: GeomPoint X=9.625 Y=2.8 Z=0
    g9: GeomPoint X=36.335 Y=2.8 Z=0
  constraints (26):
    c: Coincident(g0,g1)
    c: Coincident(g1,g2)
    c: Coincident(g2,g3)
    c: Coincident(g3,g0)
    c: Horizontal(g0)
    c: Horizontal(g2)
    c: Vertical(g1)
    c: Vertical(g3)
    c: Coincident(g4,g5)
    c: Coincident(g5,g6)
    c: Coincident(g6,g7)
    c: Coincident(g7,g4)
    c: Horizontal(g4)
    c: Horizontal(g6)
    c: Vertical(g5)
    c: Vertical(g7)
    c: Symmetric(g0,g1,g8)
    c: Symmetric(g4,g5,g9)
    c: DistanceX(g4,g4) = 6
    c: DistanceY(g5,g5) = 2.5
    c: Equal(g5,g1)
    c: Equal(g4,g0)
    c: DistanceX(g-3,g8) = 5.625
    c: DistanceX(g9,g-3) = 5.625
    c: DistanceY(g-3,g8) = 1
    c: DistanceY(g-3,g9) = 1
FEATURE [PartDesign::Pad] Pad025
  BaseFeature = -> Pad024
  Direction = (1,0,0)
  Length = 1
  Length2 = 10
  Placement = pos=(0,0,-0.8) rot=(0,0,1;0rad)
  Profile = -> Sketch036
  ReferenceAxis = -> Sketch036 [N_Axis]
  Type = 0
FEATURE [Sketcher::SketchObject] Sketch037
  ExternalGeometry = -> [ShapeBinder006]
  FullyConstrained = true
  MapMode = 5
  Placement = pos=(0,42.16,-0.8) rot=(1,0,0;1.5708rad)
  Support = -> [Pad025]
  sketch-geometry (6):
    g0: LineSegment StartX=6.9 StartY=2.8 StartZ=0 EndX=26.9 EndY=2.8 EndZ=0
    g1: LineSegment StartX=26.9 StartY=2.8 StartZ=0 EndX=26.9 EndY=1.8 EndZ=0
    g2: LineSegment StartX=26.9 StartY=1.8 StartZ=0 EndX=6.9 EndY=1.8 EndZ=0
    g3: LineSegment StartX=6.9 StartY=1.8 StartZ=0 EndX=6.9 EndY=2.8 EndZ=0
    g4: LineSegment StartX=0 StartY=1.8 StartZ=0 EndX=33.8 EndY=1.8 EndZ=0
    g5: GeomPoint X=16.9 Y=1.8 Z=0
  constraints (14):
    c: Coincident(g0,g1)
    c: Coincident(g1,g2)
    c: Coincident(g2,g3)
    c: Coincident(g3,g0)
    c: Horizontal(g0)
    c: Horizontal(g2)
    c: Vertical(g1)
    c: Vertical(g3)
    c: DistanceY(g1,g1) = 1
    c: DistanceX(g0,g0) = 20
    c: Coincident(g4,g-4)
    c: Coincident(g4,g-3)
    c: Symmetric(g2,g1,g5)
    c: Symmetric(g4,g4,g5)
FEATURE [PartDesign::Pad] Pad026
  BaseFeature = -> Pad025
  Direction = (0,-1,2e-16)
  Length = 1
  Length2 = 10
  Placement = pos=(0,0,-0.8) rot=(0,0,1;0rad)
  Profile = -> Sketch037
  ReferenceAxis = -> Sketch037 [N_Axis]
  Type = 0
FEATURE [Sketcher::SketchObject] Sketch038
  ExternalGeometry = -> [ShapeBinder006]
  FullyConstrained = true
  MapMode = 5
  Placement = pos=(0,3.8,-0.8) rot=(0,0.707107,0.707107;3.14159rad)
  Support = -> [Pad026]
  sketch-geometry (9):
    g0: LineSegment StartX=-33.8 StartY=1.8 StartZ=0 EndX=0 EndY=1.8 EndZ=0
    g1: LineSegment StartX=-31.8 StartY=1.8 StartZ=0 EndX=-26.8 EndY=1.8 EndZ=0
    g2: LineSegment StartX=-26.8 StartY=1.8 StartZ=0 EndX=-26.8 EndY=2.8 EndZ=0
    g3: LineSegment StartX=-26.8 StartY=2.8 StartZ=0 EndX=-31.8 EndY=2.8 EndZ=0
    g4: LineSegment StartX=-31.8 StartY=2.8 StartZ=0 EndX=-31.8 EndY=1.8 EndZ=0
    g5: LineSegment StartX=-7 StartY=1.8 StartZ=0 EndX=-2 EndY=1.8 EndZ=0
    g6: LineSegment StartX=-2 StartY=1.8 StartZ=0 EndX=-2 EndY=2.8 EndZ=0
    g7: LineSegment StartX=-2 StartY=2.8 StartZ=0 EndX=-7 EndY=2.8 EndZ=0
    g8: LineSegment StartX=-7 StartY=2.8 StartZ=0 EndX=-7 EndY=1.8 EndZ=0
  constraints (26):
    c: Coincident(g0,g-4)
    c: Coincident(g0,g-3)
    c: Coincident(g1,g2)
    c: Coincident(g2,g3)
    c: Coincident(g3,g4)
    c: Coincident(g4,g1)
    c: Horizontal(g1)
    c: Horizontal(g3)
    c: Vertical(g2)
    c: Vertical(g4)
    c: PointOnObject(g1,g0)
    c: Coincident(g5,g6)
    c: Coincident(g6,g7)
    c: Coincident(g7,g8)
    c: Coincident(g8,g5)
    c: Horizontal(g5)
    c: Horizontal(g7)
    c: Vertical(g6)
    c: Vertical(g8)
    c: PointOnObject(g5,g0)
    c: Equal(g2,g8)
    c: Equal(g3,g7)
    c: DistanceY(g2,g2) = 1
    c: DistanceX(g3,g3) = 5
    c: DistanceX(g0,g1) = 2
    c: DistanceX(g5,g0) = 2
FEATURE [PartDesign::Pad] Pad027
  BaseFeature = -> Pad026
  Direction = (0,1,-2e-16)
  Length = 1
  Length2 = 10
  Placement = pos=(0,0,-0.8) rot=(0,0,1;0rad)
  Profile = -> Sketch038
  ReferenceAxis = -> Sketch038 [N_Axis]
  Type = 0
FEATURE [Sketcher::SketchObject] Sketch039
  ExternalGeometry = -> [Pad027]
  FullyConstrained = true
  MapMode = 5
  Placement = pos=(0,42.16,-0.8) rot=(1,0,0;1.5708rad)
  Support = -> [Pad027]
  sketch-geometry (5):
    g0: LineSegment StartX=1.9 StartY=6.5 StartZ=0 EndX=31.9 EndY=6.5 EndZ=0
    g1: LineSegment StartX=31.9 StartY=6.5 StartZ=0 EndX=31.9 EndY=5.5 EndZ=0
    g2: LineSegment StartX=31.9 StartY=5.5 StartZ=0 EndX=1.9 EndY=5.5 EndZ=0
    g3: LineSegment StartX=1.9 StartY=5.5 StartZ=0 EndX=1.9 EndY=6.5 EndZ=0
    g4: GeomPoint X=16.9 Y=6 Z=0
  constraints (13):
    c: Coincident(g0,g1)
    c: Coincident(g1,g2)
    c: Coincident(g2,g3)
    c: Coincident(g3,g0)
    c: Horizontal(g0)
    c: Horizontal(g2)
    c: Vertical(g1)
    c: Vertical(g3)
    c: DistanceY(g1,g1) = 1
    c: DistanceX(g0,g0) = 30
    c: DistanceY(g0,g-3) = 1
    c: Symmetric(g2,g0,g4)
    c: DistanceX(g-3,g0) = 2.1
FEATURE [PartDesign::Pocket] Pocket020
  BaseFeature = -> Pad027
  Direction = (0,1,-2e-16)
  Length = 1
  Length2 = 5
  Placement = pos=(0,0,-0.8) rot=(0,0,1;0rad)
  Profile = -> Sketch039
  ReferenceAxis = -> Sketch039 [N_Axis]
  Type = 0
FEATURE [Sketcher::SketchObject] Sketch040
  ExternalGeometry = -> [Pocket020]
  FullyConstrained = true
  MapMode = 5
  Placement = pos=(0,3.8,-0.8) rot=(0,0.707107,0.707107;3.14159rad)
  Support = -> [Pocket020]
  sketch-geometry (4):
    g0: LineSegment StartX=-31.9 StartY=6.5 StartZ=0 EndX=-1.9 EndY=6.5 EndZ=0
    g1: LineSegment StartX=-1.9 StartY=6.5 StartZ=0 EndX=-1.9 EndY=5.5 EndZ=0
    g2: LineSegment StartX=-1.9 StartY=5.5 StartZ=0 EndX=-31.9 EndY=5.5 EndZ=0
    g3: LineSegment StartX=-31.9 StartY=5.5 StartZ=0 EndX=-31.9 EndY=6.5 EndZ=0
  constraints (12):
    c: Coincident(g0,g1)
    c: Coincident(g1,g2)
    c: Coincident(g2,g3)
    c: Coincident(g3,g0)
    c: Horizontal(g0)
    c: Horizontal(g2)
    c: Vertical(g1)
    c: Vertical(g3)
    c: DistanceX(g0,g0) = 30
    c: DistanceY(g1,g1) = 1
    c: DistanceX(g-3,g0) = 2.1
    c: DistanceY(g0,g-3) = 1
FEATURE [PartDesign::Pocket] Pocket021
  BaseFeature = -> Pocket020
  Direction = (0,-1,2e-16)
  Length = 1
  Length2 = 5
  Placement = pos=(0,0,-0.8) rot=(0,0,1;0rad)
  Profile = -> Sketch040
  ReferenceAxis = -> Sketch040 [N_Axis]
  Type = 0
FEATURE [Sketcher::SketchObject] Sketch041
  ExternalGeometry = -> [Pocket021]
  FullyConstrained = true
  MapMode = 5
  Placement = pos=(34,0,-0.8) rot=(0.57735,-0.57735,-0.57735;2.0944rad)
  Support = -> [Pocket021]
  sketch-geometry (4):
    g0: LineSegment StartX=-32.98 StartY=6.5 StartZ=0 EndX=-12.98 EndY=6.5 EndZ=0
    g1: LineSegment StartX=-12.98 StartY=6.5 StartZ=0 EndX=-12.98 EndY=5.5 EndZ=0
    g2: LineSegment StartX=-12.98 StartY=5.5 StartZ=0 EndX=-32.98 EndY=5.5 EndZ=0
    g3: LineSegment StartX=-32.98 StartY=5.5 StartZ=0 EndX=-32.98 EndY=6.5 EndZ=0
  constraints (12):
    c: Coincident(g0,g1)
    c: Coincident(g1,g2)
    c: Coincident(g2,g3)
    c: Coincident(g3,g0)
    c: Horizontal(g0)
    c: Horizontal(g2)
    c: Vertical(g1)
    c: Vertical(g3)
    c: DistanceY(g1,g1) = 1
    c: DistanceX(g0,g0) = 20
    c: DistanceY(g0,g-3) = 1
    c: DistanceX(g-3,g0) = 2.05
FEATURE [PartDesign::Pocket] Pocket022
  BaseFeature = -> Pocket021
  Direction = (1,0,0)
  Length = 1
  Length2 = 5
  Placement = pos=(0,0,-0.8) rot=(0,0,1;0rad)
  Profile = -> Sketch041
  ReferenceAxis = -> Sketch041 [N_Axis]
  Type = 0
FEATURE [Sketcher::SketchObject] Sketch042
  ExternalGeometry = -> [Pocket022]
  FullyConstrained = true
  MapMode = 5
  Placement = pos=(-0.2,0,-0.8) rot=(0.57735,0.57735,0.57735;2.0944rad)
  Support = -> [Pocket022]
  sketch-geometry (4):
    g0: LineSegment StartX=12.98 StartY=6.5 StartZ=0 EndX=32.98 EndY=6.5 EndZ=0
    g1: LineSegment StartX=32.98 StartY=6.5 StartZ=0 EndX=32.98 EndY=5.5 EndZ=0
    g2: LineSegment StartX=32.98 StartY=5.5 StartZ=0 EndX=12.98 EndY=5.5 EndZ=0
    g3: LineSegment StartX=12.98 StartY=5.5 StartZ=0 EndX=12.98 EndY=6.5 EndZ=0
  constraints (12):
    c: Coincident(g0,g1)
    c: Coincident(g1,g2)
    c: Coincident(g2,g3)
    c: Coincident(g3,g0)
    c: Horizontal(g0)
    c: Horizontal(g2)
    c: Vertical(g1)
    c: Vertical(g3)
    c: DistanceX(g0,g0) = 20
    c: DistanceY(g3,g3) = 1
    c: DistanceY(g0,g-3) = 1
    c: DistanceX(g0,g-3) = 2.05
FEATURE [PartDesign::Pocket] Pocket023
  BaseFeature = -> Pocket022
  Direction = (-1,0,0)
  Length = 1
  Length2 = 5
  Placement = pos=(0,0,-0.8) rot=(0,0,1;0rad)
  Profile = -> Sketch042
  ReferenceAxis = -> Sketch042 [N_Axis]
  Type = 0
FEATURE [PartDesign::Plane] DatumPlane003
  Length = 73.5102
  MapMode = 5
  Placement = pos=(0,0,6.7) rot=(0,0,1;0rad)
  ResizeMode = 0
  Width = 81.6702
FEATURE [PartDesign::ShapeBinder] ShapeBinder007
  Placement = pos=(0,0,-0.8) rot=(0,0,1;0rad)
  Support = -> [Pocket023]
  TraceSupport = false
FEATURE [Sketcher::SketchObject] Sketch043
  ExternalGeometry = -> [ShapeBinder007]
  FullyConstrained = true
  MapMode = 5
  Placement = pos=(0,0,6.7) rot=(0,0,1;0rad)
  Support = -> [DatumPlane003]
  sketch-geometry (4):
    g0: LineSegment StartX=-1.8 StartY=43.76 StartZ=0 EndX=35.6 EndY=43.76 EndZ=0
    g1: LineSegment StartX=35.6 StartY=43.76 StartZ=0 EndX=35.6 EndY=2.2 EndZ=0
    g2: LineSegment StartX=35.6 StartY=2.2 StartZ=0 EndX=-1.8 EndY=2.2 EndZ=0
    g3: LineSegment StartX=-1.8 StartY=2.2 StartZ=0 EndX=-1.8 EndY=43.76 EndZ=0
  constraints (10):
    c: Coincident(g0,g1)
    c: Coincident(g1,g2)
    c: Coincident(g2,g3)
    c: Coincident(g3,g0)
    c: Horizontal(g0)
    c: Horizontal(g2)
    c: Vertical(g1)
    c: Vertical(g3)
    c: Coincident(g0,g-3)
    c: Coincident(g1,g-4)
FEATURE [PartDesign::Pad] Pad028
  Direction = (0,0,1)
  Length = 4
  Length2 = 10
  Placement = pos=(0,0,6.7) rot=(0,0,1;0rad)
  Profile = -> Sketch043
  ReferenceAxis = -> Sketch043 [N_Axis]
  Type = 0
FEATURE [Sketcher::SketchObject] Sketch044
  ExternalGeometry = -> [ShapeBinder007]
  FullyConstrained = true
  MapMode = 5
  Placement = pos=(0,0,6.7) rot=(1,0,0;3.14159rad)
  Support = -> [Pad028]
  sketch-geometry (4):
    g0: LineSegment StartX=-0.2 StartY=-3.8 StartZ=0 EndX=34 EndY=-3.8 EndZ=0
    g1: LineSegment StartX=34 StartY=-3.8 StartZ=0 EndX=34 EndY=-42.16 EndZ=0
    g2: LineSegment StartX=34 StartY=-42.16 StartZ=0 EndX=-0.2 EndY=-42.16 EndZ=0
    g3: LineSegment StartX=-0.2 StartY=-42.16 StartZ=0 EndX=-0.2 EndY=-3.8 EndZ=0
  constraints (10):
    c: Coincident(g0,g1)
    c: Coincident(g1,g2)
    c: Coincident(g2,g3)
    c: Coincident(g3,g0)
    c: Horizontal(g0)
    c: Horizontal(g2)
    c: Vertical(g1)
    c: Vertical(g3)
    c: Coincident(g0,g-3)
    c: Coincident(g1,g-4)
FEATURE [PartDesign::Pad] Pad029
  BaseFeature = -> Pad028
  Direction = (0,0,-1)
  Length = 2
  Length2 = 10
  Placement = pos=(0,0,6.7) rot=(0,0,1;0rad)
  Profile = -> Sketch044
  ReferenceAxis = -> Sketch044 [N_Axis]
  Type = 0
FEATURE [Sketcher::SketchObject] Sketch045
  ExternalGeometry = -> [Pad029]
  FullyConstrained = true
  MapMode = 5
  Placement = pos=(0,0,4.7) rot=(1,0,0;3.14159rad)
  Support = -> [Pad029]
  sketch-geometry (4):
    g0: LineSegment StartX=0.8 StartY=-4.8 StartZ=0 EndX=33 EndY=-4.8 EndZ=0
    g1: LineSegment StartX=33 StartY=-4.8 StartZ=0 EndX=33 EndY=-41.16 EndZ=0
    g2: LineSegment StartX=33 StartY=-41.16 StartZ=0 EndX=0.8 EndY=-41.16 EndZ=0
    g3: LineSegment StartX=0.8 StartY=-41.16 StartZ=0 EndX=0.8 EndY=-4.8 EndZ=0
  constraints (12):
    c: Coincident(g0,g1)
    c: Coincident(g1,g2)
    c: Coincident(g2,g3)
    c: Coincident(g3,g0)
    c: Horizontal(g0)
    c: Horizontal(g2)
    c: Vertical(g1)
    c: Vertical(g3)
    c: DistanceX(g-3,g0) = 1
    c: DistanceX(g1,g-4) = 1
    c: DistanceY(g-4,g1) = 1
    c: DistanceY(g0,g-3) = 1
FEATURE [PartDesign::Pocket] Pocket024
  BaseFeature = -> Pad029
  Direction = (0,0,1)
  Length = 5
  Length2 = 5
  Placement = pos=(0,0,6.7) rot=(0,0,1;0rad)
  Profile = -> Sketch045
  ReferenceAxis = -> Sketch045 [N_Axis]
  Type = 0
FEATURE [Sketcher::SketchObject] Sketch046
  ExternalGeometry = -> [Pocket024]
  FullyConstrained = true
  MapMode = 5
  Placement = pos=(0,42.16,6.7) rot=(0,0.707107,0.707107;3.14159rad)
  Support = -> [Pocket024]
  sketch-geometry (4):
    g0: LineSegment StartX=-29.4 StartY=-1.9 StartZ=0 EndX=-4.4 EndY=-1.9 EndZ=0
    g1: LineSegment StartX=-4.4 StartY=-1.9 StartZ=0 EndX=-4.4 EndY=-1.1 EndZ=0
    g2: LineSegment StartX=-4.4 StartY=-1.1 StartZ=0 EndX=-29.4 EndY=-1.1 EndZ=0
    g3: LineSegment StartX=-29.4 StartY=-1.1 StartZ=0 EndX=-29.4 EndY=-1.9 EndZ=0
  constraints (12):
    c: Coincident(g0,g1)
    c: Coincident(g1,g2)
    c: Coincident(g2,g3)
    c: Coincident(g3,g0)
    c: Horizontal(g0)
    c: Horizontal(g2)
    c: Vertical(g1)
    c: Vertical(g3)
    c: DistanceY(g0,g2) = 0.8
    c: DistanceY(g-3,g0) = 0.1
    c: DistanceX(g2,g2) = 25
    c: DistanceX(g-5,g0) = 4.6
FEATURE [PartDesign::Pad] Pad030
  BaseFeature = -> Pocket024
  Direction = (0,1,-2e-16)
  Length = 0.5
  Length2 = 10
  Placement = pos=(0,0,6.7) rot=(0,0,1;0rad)
  Profile = -> Sketch046
  ReferenceAxis = -> Sketch046 [N_Axis]
  Type = 0
FEATURE [Sketcher::SketchObject] Sketch047
  ExternalGeometry = -> [Pad030]
  FullyConstrained = true
  MapMode = 5
  Placement = pos=(-0.2,0,6.7) rot=(0.57735,-0.57735,-0.57735;2.0944rad)
  Support = -> [Pad030]
  sketch-geometry (4):
    g0: LineSegment StartX=-30.5 StartY=-1.1 StartZ=0 EndX=-15.5 EndY=-1.1 EndZ=0
    g1: LineSegment StartX=-15.5 StartY=-1.1 StartZ=0 EndX=-15.5 EndY=-1.9 EndZ=0
    g2: LineSegment StartX=-15.5 StartY=-1.9 StartZ=0 EndX=-30.5 EndY=-1.9 EndZ=0
    g3: LineSegment StartX=-30.5 StartY=-1.9 StartZ=0 EndX=-30.5 EndY=-1.1 EndZ=0
  constraints (12):
    c: Coincident(g0,g1)
    c: Coincident(g1,g2)
    c: Coincident(g2,g3)
    c: Coincident(g3,g0)
    c: Horizontal(g0)
    c: Horizontal(g2)
    c: Vertical(g1)
    c: Vertical(g3)
    c: DistanceY(g1,g1) = 0.8
    c: DistanceY(g-3,g2) = 0.1
    c: DistanceX(g0,g0) = 15
    c: DistanceX(g0,g-3) = 11.7
FEATURE [Sketcher::SketchObject] Sketch048
  ExternalGeometry = -> [Pocket023]
  FullyConstrained = true
  MapMode = 5
  Placement = pos=(0,2.2,-0.8) rot=(1,0,0;1.5708rad)
  Support = -> [Pocket023]
  sketch-geometry (5):
    g0: LineSegment StartX=2.9 StartY=7.5 StartZ=0 EndX=30.9 EndY=7.5 EndZ=0
    g1: LineSegment StartX=30.9 StartY=7.5 StartZ=0 EndX=30.9 EndY=2.5 EndZ=0
    g2: LineSegment StartX=30.9 StartY=2.5 StartZ=0 EndX=2.9 EndY=2.5 EndZ=0
    g3: LineSegment StartX=2.9 StartY=2.5 StartZ=0 EndX=2.9 EndY=7.5 EndZ=0
    g4: GeomPoint X=16.9 Y=7.5 Z=0
  constraints (12):
    c: Coincident(g0,g1)
    c: Coincident(g1,g2)
    c: Coincident(g2,g3)
    c: Coincident(g3,g0)
    c: Horizontal(g0)
    c: Horizontal(g2)
    c: Vertical(g1)
    c: Vertical(g3)
    c: DistanceX(g0,g0) = 28
    c: DistanceY(g1,g1) = 5
    c: Symmetric(g0,g0,g4)
    c: Symmetric(g-3,g-3,g4)
FEATURE [PartDesign::Pad] Pad031
  BaseFeature = -> Pocket023
  Direction = (0,-1,2e-16)
  Length = 6.4
  Length2 = 10
  Placement = pos=(0,0,-0.8) rot=(0,0,1;0rad)
  Profile = -> Sketch048
  ReferenceAxis = -> Sketch048 [N_Axis]
  Type = 0
FEATURE [Sketcher::SketchObject] Sketch049
  ExternalGeometry = -> [Pad031]
  FullyConstrained = true
  MapMode = 5
  Placement = pos=(0,1.7e-15,6.7) rot=(0,0,1;0rad)
  Support = -> [Pad031]
  sketch-geometry (4):
    g0: LineSegment StartX=4.9 StartY=2.2 StartZ=0 EndX=28.9 EndY=2.2 EndZ=0
    g1: LineSegment StartX=28.9 StartY=2.2 StartZ=0 EndX=28.9 EndY=-3.3 EndZ=0
    g2: LineSegment StartX=28.9 StartY=-3.3 StartZ=0 EndX=4.9 EndY=-3.3 EndZ=0
    g3: LineSegment StartX=4.9 StartY=-3.3 StartZ=0 EndX=4.9 EndY=2.2 EndZ=0
  constraints (12):
    c: Coincident(g0,g1)
    c: Coincident(g1,g2)
    c: Coincident(g2,g3)
    c: Coincident(g3,g0)
    c: Horizontal(g0)
    c: Horizontal(g2)
    c: Vertical(g1)
    c: Vertical(g3)
    c: PointOnObject(g0,g-3)
    c: DistanceX(g0,g0) = 24
    c: DistanceX(g-3,g0) = 2
    c: DistanceY(g1,g1) = 5.5
FEATURE [PartDesign::Pocket] Pocket025
  BaseFeature = -> Pad031
  Direction = (0,-2e-16,-1)
  Length = 4
  Length2 = 5
  Placement = pos=(0,0,-0.8) rot=(0,0,1;0rad)
  Profile = -> Sketch049
  ReferenceAxis = -> Sketch049 [N_Axis]
  Type = 0
FEATURE [Sketcher::SketchObject] Sketch050
  ExternalGeometry = -> [Pocket025]
  FullyConstrained = true
  MapMode = 5
  Placement = pos=(30.9,0,-0.8) rot=(0.57735,0.57735,0.57735;2.0944rad)
  Support = -> [Pocket025]
  sketch-geometry (1):
    g0: Circle CenterX=-0.55 CenterY=6.2 CenterZ=0 NormalX=0 NormalY=0 NormalZ=1 AngleXU=0 Radius=0.6
  constraints (3):
    c: Diameter(g0) = 1.2
    c: DistanceY(g0,g-3) = 1.3
    c: DistanceX(g0,g-3) = 2.75
FEATURE [PartDesign::Pocket] Pocket026
  BaseFeature = -> Pocket025
  Direction = (-1,0,0)
  Length = 5
  Length2 = 5
  Placement = pos=(0,0,-0.8) rot=(0,0,1;0rad)
  Profile = -> Sketch050
  ReferenceAxis = -> Sketch050 [N_Axis]
  Type = 1
FEATURE [Sketcher::SketchObject] Sketch051
  ExternalGeometry = -> [Pad031]
  FullyConstrained = true
  MapMode = 5
  Placement = pos=(0,43.76,-0.8) rot=(0,0.707107,0.707107;3.14159rad)
  Support = -> [Pad031]
  sketch-geometry (5):
    g0: LineSegment StartX=-30.9 StartY=7.5 StartZ=0 EndX=-2.9 EndY=7.5 EndZ=0
    g1: LineSegment StartX=-2.9 StartY=7.5 StartZ=0 EndX=-2.9 EndY=2.5 EndZ=0
    g2: LineSegment StartX=-2.9 StartY=2.5 StartZ=0 EndX=-30.9 EndY=2.5 EndZ=0
    g3: LineSegment StartX=-30.9 StartY=2.5 StartZ=0 EndX=-30.9 EndY=7.5 EndZ=0
    g4: GeomPoint X=-16.9 Y=7.5 Z=0
  constraints (12):
    c: Coincident(g0,g1)
    c: Coincident(g1,g2)
    c: Coincident(g2,g3)
    c: Coincident(g3,g0)
    c: Horizontal(g0)
    c: Horizontal(g2)
    c: Vertical(g1)
    c: Vertical(g3)
    c: DistanceX(g0,g0) = 28
    c: DistanceY(g1,g1) = 5
    c: Symmetric(g0,g0,g4)
    c: Symmetric(g-3,g-3,g4)
FEATURE [PartDesign::Pad] Pad032
  BaseFeature = -> Pocket026
  Direction = (0,1,-2e-16)
  Length = 6.4
  Length2 = 10
  Placement = pos=(0,0,-0.8) rot=(0,0,1;0rad)
  Profile = -> Sketch051
  ReferenceAxis = -> Sketch051 [N_Axis]
  Type = 0
FEATURE [Sketcher::SketchObject] Sketch052
  ExternalGeometry = -> [Pad032]
  FullyConstrained = true
  MapMode = 5
  Placement = pos=(0,1.7e-15,6.7) rot=(0,0,1;0rad)
  Support = -> [Pad032]
  sketch-geometry (5):
    g0: LineSegment StartX=4.9 StartY=49.26 StartZ=0 EndX=28.9 EndY=49.26 EndZ=0
    g1: LineSegment StartX=28.9 StartY=49.26 StartZ=0 EndX=28.9 EndY=43.76 EndZ=0
    g2: LineSegment StartX=28.9 StartY=43.76 StartZ=0 EndX=4.9 EndY=43.76 EndZ=0
    g3: LineSegment StartX=4.9 StartY=43.76 StartZ=0 EndX=4.9 EndY=49.26 EndZ=0
    g4: GeomPoint X=16.9 Y=43.76 Z=0
  constraints (12):
    c: Coincident(g0,g1)
    c: Coincident(g1,g2)
    c: Coincident(g2,g3)
    c: Coincident(g3,g0)
    c: Horizontal(g0)
    c: Horizontal(g2)
    c: Vertical(g1)
    c: Vertical(g3)
    c: DistanceX(g2,g2) = 24
    c: DistanceY(g1,g1) = 5.5
    c: Symmetric(g2,g1,g4)
    c: Symmetric(g-3,g-3,g4)
FEATURE [PartDesign::Pocket] Pocket027
  BaseFeature = -> Pad032
  Direction = (0,-2e-16,-1)
  Length = 4
  Length2 = 5
  Placement = pos=(0,0,-0.8) rot=(0,0,1;0rad)
  Profile = -> Sketch052
  ReferenceAxis = -> Sketch052 [N_Axis]
  Type = 0
FEATURE [Sketcher::SketchObject] Sketch053
  ExternalGeometry = -> [Pocket027]
  FullyConstrained = true
  MapMode = 5
  Placement = pos=(2.9,0,-0.8) rot=(0.57735,-0.57735,-0.57735;2.0944rad)
  Support = -> [Pocket027]
  sketch-geometry (1):
    g0: Circle CenterX=-46.51 CenterY=6.2 CenterZ=0 NormalX=0 NormalY=0 NormalZ=1 AngleXU=0 Radius=0.6
  constraints (3):
    c: Diameter(g0) = 1.2
    c: DistanceY(g0,g-3) = 1.3
    c: DistanceX(g0,g-3) = 2.75
FEATURE [PartDesign::Pocket] Pocket028
  BaseFeature = -> Pocket027
  Direction = (1,0,0)
  Length = 5
  Length2 = 5
  Placement = pos=(0,0,-0.8) rot=(0,0,1;0rad)
  Profile = -> Sketch053
  ReferenceAxis = -> Sketch053 [N_Axis]
  Type = 1
FEATURE [PartDesign::Fillet] Fillet011
  Base = -> Pocket028 [Edge10,Edge11,Edge9,Edge1,Edge2,Edge17,Edge68,Edge8]
  BaseFeature = -> Pocket028
  Placement = pos=(0,0,-0.8) rot=(0,0,1;0rad)
  Radius = 2
  SupportTransform = false
  UseAllEdges = false
FEATURE [PartDesign::Fillet] Fillet012
  Base = -> Fillet011 [Edge5,Edge80]
  BaseFeature = -> Fillet011
  Placement = pos=(0,0,-0.8) rot=(0,0,1;0rad)
  Radius = 1.8
  SupportTransform = false
  UseAllEdges = false
FEATURE [PartDesign::Fillet] Fillet013
  Base = -> Fillet012 [Edge239,Edge204]
  BaseFeature = -> Fillet012
  Placement = pos=(0,0,-0.8) rot=(0,0,1;0rad)
  Radius = 3
  SupportTransform = false
  UseAllEdges = false
FEATURE [PartDesign::Fillet] Fillet014
  Base = -> Fillet013 [Edge240,Edge64]
  BaseFeature = -> Fillet013
  Placement = pos=(0,0,-0.8) rot=(0,0,1;0rad)
  Radius = 4.8
  SupportTransform = false
  UseAllEdges = false
FEATURE [PartDesign::Fillet] Fillet015
  Base = -> Fillet014 [Edge1,Edge3,Edge2,Edge4,Edge10,Edge12,Edge14,Edge94,Edge228,Edge229,Edge97,Edge233,Edge234]
  BaseFeature = -> Fillet014
  Placement = pos=(0,0,-0.8) rot=(0,0,1;0rad)
  Radius = 0.7
  SupportTransform = false
  UseAllEdges = false
FEATURE [PartDesign::Fillet] Fillet016
  Base = -> Fillet015 [Edge306,Edge308,Edge309,Edge304,Edge303,Edge302,Edge305,Edge307,Edge293,Edge296,Edge294,Edge297,Edge292,Edge295,Edge290,Edge291,Edge240,Edge241,Edge237,Edge233,Edge239,Edge242,Edge247,Edge244,Edge246,Edge238,Edge234,Edge236,Edge245,Edge243,Edge235,Edge232]
  BaseFeature = -> Fillet015
  Placement = pos=(0,0,-0.8) rot=(0,0,1;0rad)
  Radius = 0.99
  SupportTransform = false
  UseAllEdges = false
FEATURE [PartDesign::Fillet] Fillet017
  Base = -> Fillet016 [Edge429,Edge431,Edge427,Edge432,Edge397,Edge395,Edge400,Edge399,Edge405,Edge403,Edge408,Edge407,Edge430,Edge428,Edge426,Edge425,Edge401,Edge402,Edge393,Edge394,Edge398,Edge396,Edge404,Edge406]
  BaseFeature = -> Fillet016
  Placement = pos=(0,0,-0.8) rot=(0,0,1;0rad)
  Radius = 0.49
  SupportTransform = false
  UseAllEdges = false
FEATURE [PartDesign::Fillet] Fillet018
  Base = -> Fillet017 [Edge176,Edge177,Edge179,Edge181]
  BaseFeature = -> Fillet017
  Placement = pos=(0,0,-0.8) rot=(0,0,1;0rad)
  Radius = 1.5
  SupportTransform = false
  UseAllEdges = false
FEATURE [PartDesign::Body] Body006  label="Case-Top-X"
  Group = -> [ShapeBinder004,Sketch030,ShapeBinder005,ShapeBinder006,Pad023,Sketch031,Pocket016,Sketch032,Pocket017,Sketch033,Pocket018,Sketch034,Pocket019,Sketch035,Pad024,Sketch036,Pad025,Sketch037,Pad026,Sketch038,Pad027,Sketch039,Pocket020,Sketch040,Pocket021,Sketch041,Pocket022,Sketch042,Pocket023,Sketch048,Pad031,Sketch049,Pocket025,Sketch050,Pocket026,Sketch051,Pad032,Sketch052,Pocket027,Sketch053,+9 more]
  Origin = -> Origin134
  Tip = -> Fillet018
FEATURE [PartDesign::Pad] Pad033
  BaseFeature = -> Pad030
  Direction = (-1,0,0)
  Length = 0.5
  Length2 = 10
  Placement = pos=(0,0,6.7) rot=(0,0,1;0rad)
  Profile = -> Sketch047
  ReferenceAxis = -> Sketch047 [N_Axis]
  Type = 0
FEATURE [Sketcher::SketchObject] Sketch054
  ExternalGeometry = -> [Pad033]
  FullyConstrained = true
  MapMode = 5
  Placement = pos=(34,0,6.7) rot=(0.57735,0.57735,0.57735;2.0944rad)
  Support = -> [Pad033]
  sketch-geometry (4):
    g0: LineSegment StartX=15.51 StartY=-1.1 StartZ=0 EndX=30.51 EndY=-1.1 EndZ=0
    g1: LineSegment StartX=30.51 StartY=-1.1 StartZ=0 EndX=30.51 EndY=-1.9 EndZ=0
    g2: LineSegment StartX=30.51 StartY=-1.9 StartZ=0 EndX=15.51 EndY=-1.9 EndZ=0
    g3: LineSegment StartX=15.51 StartY=-1.9 StartZ=0 EndX=15.51 EndY=-1.1 EndZ=0
  constraints (12):
    c: Coincident(g0,g1)
    c: Coincident(g1,g2)
    c: Coincident(g2,g3)
    c: Coincident(g3,g0)
    c: Horizontal(g0)
    c: Horizontal(g2)
    c: Vertical(g1)
    c: Vertical(g3)
    c: DistanceY(g3,g3) = 0.8
    c: DistanceY(g-3,g2) = 0.1
    c: DistanceX(g0,g0) = 15
    c: DistanceX(g1,g-3) = 11.65
FEATURE [PartDesign::Pad] Pad034
  BaseFeature = -> Pad033
  Direction = (1,0,0)
  Length = 0.5
  Length2 = 10
  Placement = pos=(0,0,6.7) rot=(0,0,1;0rad)
  Profile = -> Sketch054
  ReferenceAxis = -> Sketch054 [N_Axis]
  Type = 0
FEATURE [Sketcher::SketchObject] Sketch055
  ExternalGeometry = -> [Pad034]
  FullyConstrained = true
  MapMode = 5
  Placement = pos=(0,3.8,6.7) rot=(1,0,0;1.5708rad)
  Support = -> [Pad034]
  sketch-geometry (4):
    g0: LineSegment StartX=4.4 StartY=-1.1 StartZ=0 EndX=29.4 EndY=-1.1 EndZ=0
    g1: LineSegment StartX=29.4 StartY=-1.1 StartZ=0 EndX=29.4 EndY=-1.9 EndZ=0
    g2: LineSegment StartX=29.4 StartY=-1.9 StartZ=0 EndX=4.4 EndY=-1.9 EndZ=0
    g3: LineSegment StartX=4.4 StartY=-1.9 StartZ=0 EndX=4.4 EndY=-1.1 EndZ=0
  constraints (12):
    c: Coincident(g0,g1)
    c: Coincident(g1,g2)
    c: Coincident(g2,g3)
    c: Coincident(g3,g0)
    c: Horizontal(g0)
    c: Horizontal(g2)
    c: Vertical(g1)
    c: Vertical(g3)
    c: DistanceY(g1,g1) = 0.8
    c: DistanceY(g-3,g2) = 0.1
    c: DistanceX(g0,g0) = 25
    c: DistanceX(g-3,g2) = 4.6
FEATURE [PartDesign::Pad] Pad035
  BaseFeature = -> Pad034
  Direction = (0,-1,2e-16)
  Length = 0.5
  Length2 = 10
  Placement = pos=(0,0,6.7) rot=(0,0,1;0rad)
  Profile = -> Sketch055
  ReferenceAxis = -> Sketch055 [N_Axis]
  Type = 0
FEATURE [PartDesign::Fillet] Fillet019
  Base = -> Pad035 [Edge57,Edge59,Edge60,Edge56,Edge53,Edge55,Edge54,Edge58,Edge50,Edge48,Edge51,Edge49,Edge52,Edge46,Edge45,Edge47,Edge74,Edge72,Edge75,Edge73,Edge76,Edge71,Edge70,Edge69,Edge64,Edge62,Edge65,Edge63,Edge67,Edge66,Edge68,Edge61]
  BaseFeature = -> Pad035
  Placement = pos=(0,0,6.7) rot=(0,0,1;0rad)
  Radius = 0.39
  SupportTransform = false
  UseAllEdges = false
FEATURE [PartDesign::Fillet] Fillet020
  Base = -> Fillet019 [Edge37,Edge60,Edge12,Edge9]
  BaseFeature = -> Fillet019
  Placement = pos=(0,0,6.7) rot=(0,0,1;0rad)
  Radius = 1
  SupportTransform = false
  UseAllEdges = false
FEATURE [PartDesign::Fillet] Fillet021
  Base = -> Fillet020 [Edge86,Edge88,Edge87,Edge84,Edge85,Edge83,Edge82,Edge81]
  BaseFeature = -> Fillet020
  Placement = pos=(0,0,6.7) rot=(0,0,1;0rad)
  Radius = 2
  SupportTransform = false
  UseAllEdges = false
FEATURE [PartDesign::Body] Body007  label="Case-Bottom-X"
  Group = -> [DatumPlane003,ShapeBinder007,Sketch043,Pad028,Sketch044,Pad029,Sketch045,Pocket024,Sketch046,Pad030,Sketch047,Pad033,Sketch054,Pad034,Sketch055,Pad035,Fillet019,Fillet020,Fillet021]
  Origin = -> Origin150
  Tip = -> Fillet021
FEATURE [Part::Feature] Part__Feature071  label="Kapton Tape"
  Placement = pos=(0.0491885,1.18055,-6e-16) rot=(0,0,1;3.14159rad)
  shape: bbox 20.06 x 3.981 x 9.27 mm, 32 faces (baked)
FEATURE [Part::Feature] Part__Feature072  label="Battery Cell"
  Placement = pos=(0,1e-16,0) rot=(0,0,1;0rad)
  shape: bbox 20.13 x 4.449 x 33.22 mm, 70 faces (baked)
FEATURE [Part::Feature] Part__Feature073  label="Board Part 1"
  Placement = pos=(0,1e-16,0) rot=(0,0,1;0rad)
  shape: bbox 0.9244 x 0.616 x 1.78 mm, 6 faces (baked)
FEATURE [Part::Feature] Part__Feature074  label="PCB"
  Placement = pos=(0,1e-16,0) rot=(0,0,1;0rad)
  shape: bbox 17.16 x 0.7 x 2.9 mm, 6 faces (baked)
FEATURE [Part::Feature] Part__Feature075  label="Positive"
  Placement = pos=(3.04919,1.18055,-7e-16) rot=(0,0,1;3.14159rad)
  shape: bbox 20.74 x 1.07 x 17.24 mm, 7 faces (baked)
FEATURE [Part::Feature] Part__Feature076  label="Negative"
  Placement = pos=(3.04919,1.18055,-7e-16) rot=(0,0,1;3.14159rad)
  shape: bbox 21.08 x 1.07 x 13.22 mm, 7 faces (baked)
FEATURE [Part::Feature] Part__Feature077  label="Board Part 2"
  Placement = pos=(0,1e-16,0) rot=(0,0,1;0rad)
  shape: bbox 0.6625 x 0.616 x 1.78 mm, 6 faces (baked)
FEATURE [App::Part] Battery402030_v3  label="Battery402030 v3"
  Group = -> [Part__Feature071,Part__Feature072,Part__Feature073,Part__Feature074,Part__Feature075,Part__Feature076,Part__Feature077]
  Origin = -> Origin151
  Placement = pos=(19.4,7.95,8.35) rot=(-1,0,0;1.5708rad)
